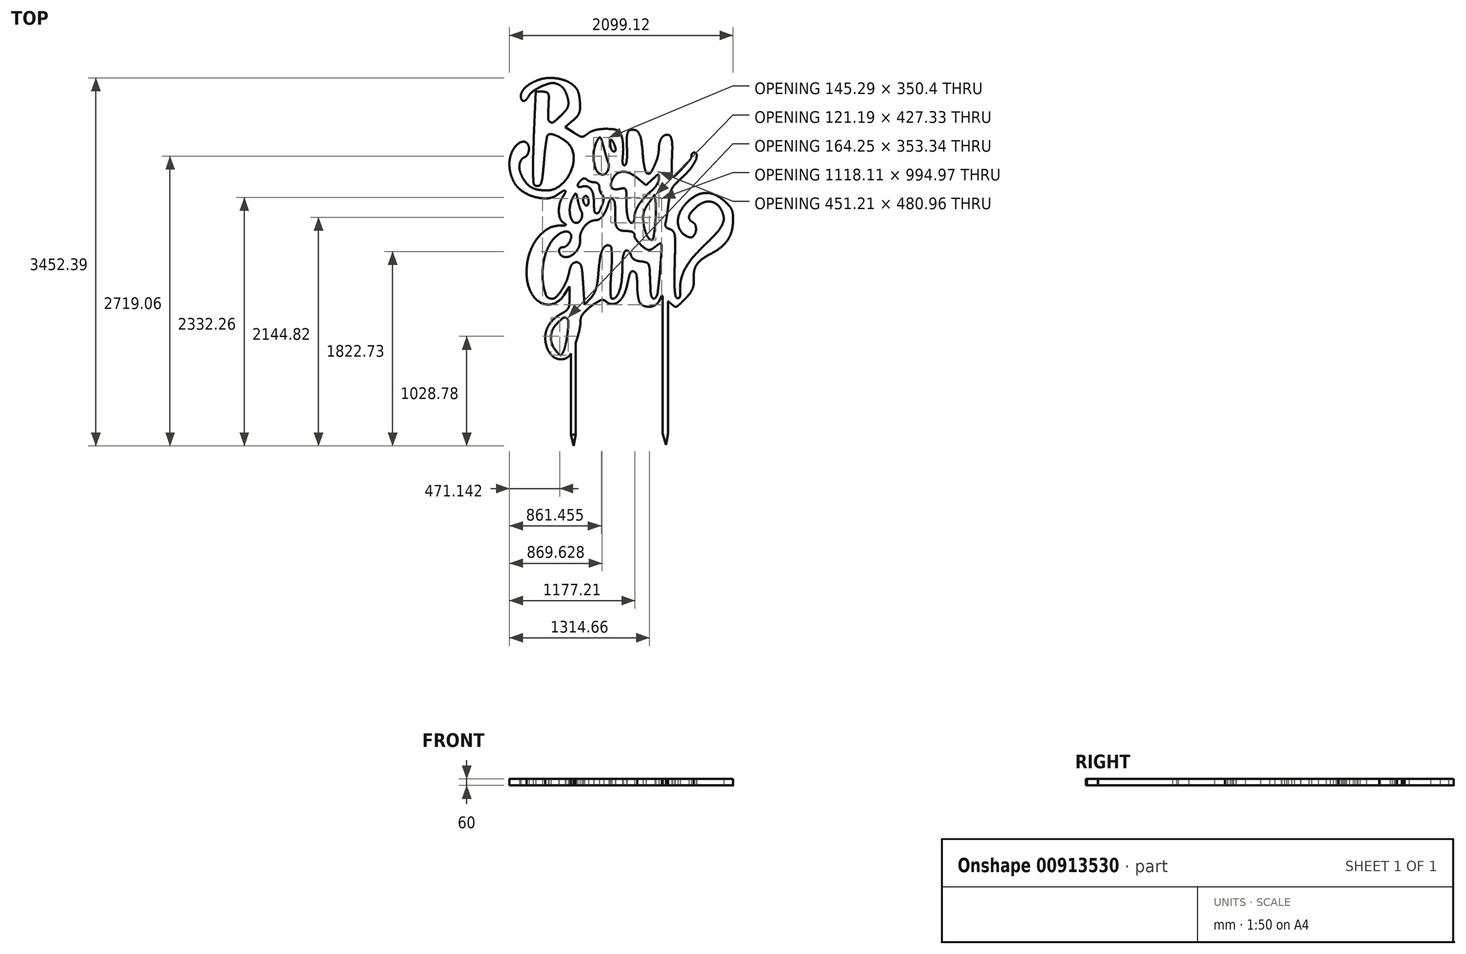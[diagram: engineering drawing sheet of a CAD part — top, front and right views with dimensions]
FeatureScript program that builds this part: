
annotation { "Feature Type Name" : "Feature", "Feature Type Description" : "" }
export const myFeature = defineFeature(function(context is Context, id is Id, definition is map)
    precondition{}
    {
        {
            var Q0;
            Q0=qCreatedBy(makeId("Top.planeOp"),FACE);
            var sketch = newSketch(context, id + "F0", { "sketchPlane" : qUnion([Q0])});
            skArc(sketch, "E0", {"start": v(-777.04, 1301.74) * mm, "mid": v(-811.98, 1287.44) * mm, "end": v(-845.72, 1270.53) * mm});
            skArc(sketch, "E1", {"start": v(-845.72, 1270.53) * mm, "mid": v(-872.99, 1253.32) * mm, "end": v(-897.97, 1232.95) * mm});
            skArc(sketch, "E2", {"start": v(-897.97, 1232.95) * mm, "mid": v(-916, 1213.6) * mm, "end": v(-930.89, 1191.73) * mm});
            skArc(sketch, "E3", {"start": v(-930.89, 1191.73) * mm, "mid": v(-939.28, 1171.38) * mm, "end": v(-942.14, 1149.56) * mm});
            skArc(sketch, "E4", {"start": v(-942.14, 1149.56) * mm, "mid": v(-940.45, 1132.62) * mm, "end": v(-935.44, 1116.36) * mm});
            skArc(sketch, "E5", {"start": v(-935.44, 1116.36) * mm, "mid": v(-928.12, 1107.56) * mm, "end": v(-917.15, 1104.32) * mm});
            skArc(sketch, "E6", {"start": v(-917.15, 1104.32) * mm, "mid": v(-903.56, 1107.28) * mm, "end": v(-892.28, 1115.43) * mm});
            skArc(sketch, "E7", {"start": v(-892.28, 1115.43) * mm, "mid": v(-878.92, 1132.04) * mm, "end": v(-867.72, 1150.18) * mm});
            skArc(sketch, "E8", {"start": v(-867.72, 1150.18) * mm, "mid": v(-849.95, 1175.64) * mm, "end": v(-826.74, 1196.26) * mm});
            skArc(sketch, "E9", {"start": v(-826.74, 1196.26) * mm, "mid": v(-789.65, 1219.77) * mm, "end": v(-750.67, 1240) * mm});
            skArc(sketch, "E10", {"start": v(-750.67, 1240) * mm, "mid": v(-710.75, 1256.5) * mm, "end": v(-669.57, 1269.54) * mm});
            skArc(sketch, "E11", {"start": v(-669.57, 1269.54) * mm, "mid": v(-641.49, 1272.95) * mm, "end": v(-613.58, 1268.31) * mm});
            skArc(sketch, "E12", {"start": v(-613.58, 1268.31) * mm, "mid": v(-592.46, 1259.99) * mm, "end": v(-572.66, 1248.88) * mm});
            skArc(sketch, "E13", {"start": v(-572.66, 1248.88) * mm, "mid": v(-556.03, 1235.87) * mm, "end": v(-541.82, 1220.25) * mm});
            skArc(sketch, "E14", {"start": v(-541.82, 1220.25) * mm, "mid": v(-528.73, 1200.4) * mm, "end": v(-518.57, 1178.9) * mm});
            skArc(sketch, "E15", {"start": v(-518.57, 1178.9) * mm, "mid": v(-508.48, 1150.04) * mm, "end": v(-500.37, 1120.57) * mm});
            skArc(sketch, "E16", {"start": v(-500.37, 1120.57) * mm, "mid": v(-496.82, 1100.94) * mm, "end": v(-495.47, 1081.04) * mm});
            skArc(sketch, "E17", {"start": v(-495.47, 1081.04) * mm, "mid": v(-496.88, 1064.6) * mm, "end": v(-501.45, 1048.76) * mm});
            skArc(sketch, "E18", {"start": v(-501.45, 1048.76) * mm, "mid": v(-509.77, 1031.76) * mm, "end": v(-520.6, 1016.25) * mm});
            skArc(sketch, "E19", {"start": v(-520.6, 1016.25) * mm, "mid": v(-539, 994.92) * mm, "end": v(-558.41, 974.52) * mm});
            skArc(sketch, "E20", {"start": v(-558.41, 974.52) * mm, "mid": v(-594.13, 940.44) * mm, "end": v(-631.42, 908.07) * mm});
            skArc(sketch, "E21", {"start": v(-631.42, 908.07) * mm, "mid": v(-648.14, 901.21) * mm, "end": v(-665.8, 905.07) * mm});
            skArc(sketch, "E22", {"start": v(-665.8, 905.07) * mm, "mid": v(-679.62, 918.6) * mm, "end": v(-684.95, 937.2) * mm});
            skArc(sketch, "E23", {"start": v(-684.95, 937.2) * mm, "mid": v(-685.1, 991.39) * mm, "end": v(-683.23, 1045.54) * mm});
            skArc(sketch, "E24", {"start": v(-683.23, 1045.54) * mm, "mid": v(-681.09, 1091.9) * mm, "end": v(-679.61, 1138.3) * mm});
            skArc(sketch, "E25", {"start": v(-679.61, 1138.3) * mm, "mid": v(-680.84, 1155.14) * mm, "end": v(-685.3, 1171.42) * mm});
            skArc(sketch, "E26", {"start": v(-685.3, 1171.42) * mm, "mid": v(-691.92, 1181.1) * mm, "end": v(-702.22, 1186.72) * mm});
            skArc(sketch, "E27", {"start": v(-702.22, 1186.72) * mm, "mid": v(-720.42, 1190.37) * mm, "end": v(-738.94, 1191.6) * mm});
            skLineSegment(sketch, "E28", {"start": v(-738.94, 1191.6) * mm, "end": v(-802.44, 1191.6) * mm});
            skLineSegment(sketch, "E29", {"start": v(-802.44, 1191.6) * mm, "end": v(-820.4, 760.61) * mm});
            skArc(sketch, "E30", {"start": v(-820.4, 760.61) * mm, "mid": v(-824.35, 656.8) * mm, "end": v(-827.57, 552.97) * mm});
            skArc(sketch, "E31", {"start": v(-827.57, 552.97) * mm, "mid": v(-828.5, 487.7) * mm, "end": v(-827.69, 422.42) * mm});
            skArc(sketch, "E32", {"start": v(-827.69, 422.42) * mm, "mid": v(-825.98, 378.55) * mm, "end": v(-823.12, 334.73) * mm});
            skArc(sketch, "E33", {"start": v(-823.12, 334.73) * mm, "mid": v(-818.8, 321.38) * mm, "end": v(-808.9, 311.44) * mm});
            skArc(sketch, "E34", {"start": v(-808.9, 311.44) * mm, "mid": v(-793.14, 305.84) * mm, "end": v(-776.47, 307.25) * mm});
            skArc(sketch, "E35", {"start": v(-776.47, 307.25) * mm, "mid": v(-762.48, 315.44) * mm, "end": v(-753.63, 329.01) * mm});
            skArc(sketch, "E36", {"start": v(-753.63, 329.01) * mm, "mid": v(-744.19, 361.14) * mm, "end": v(-738.67, 394.16) * mm});
            skArc(sketch, "E37", {"start": v(-738.67, 394.16) * mm, "mid": v(-731.22, 469.42) * mm, "end": v(-724.8, 544.78) * mm});
            skArc(sketch, "E38", {"start": v(-724.8, 544.78) * mm, "mid": v(-721.01, 589.09) * mm, "end": v(-716.56, 633.33) * mm});
            skArc(sketch, "E39", {"start": v(-716.56, 633.33) * mm, "mid": v(-711.98, 671.65) * mm, "end": v(-706.54, 709.86) * mm});
            skArc(sketch, "E40", {"start": v(-706.54, 709.86) * mm, "mid": v(-701.45, 741.63) * mm, "end": v(-695.98, 773.33) * mm});
            skArc(sketch, "E41", {"start": v(-695.98, 773.33) * mm, "mid": v(-693.15, 780.26) * mm, "end": v(-687.74, 785.44) * mm});
            skArc(sketch, "E42", {"start": v(-687.74, 785.44) * mm, "mid": v(-666.87, 792.87) * mm, "end": v(-644.78, 791.07) * mm});
            skArc(sketch, "E43", {"start": v(-644.78, 791.07) * mm, "mid": v(-609.9, 778.58) * mm, "end": v(-576.49, 762.61) * mm});
            skArc(sketch, "E44", {"start": v(-576.49, 762.61) * mm, "mid": v(-542.28, 741.75) * mm, "end": v(-510.37, 717.52) * mm});
            skArc(sketch, "E45", {"start": v(-510.37, 717.52) * mm, "mid": v(-488.03, 694.58) * mm, "end": v(-470.6, 667.72) * mm});
            skArc(sketch, "E46", {"start": v(-470.6, 667.72) * mm, "mid": v(-449.75, 607.16) * mm, "end": v(-447.14, 543.16) * mm});
            skArc(sketch, "E47", {"start": v(-447.14, 543.16) * mm, "mid": v(-462.03, 472.82) * mm, "end": v(-491.08, 407.05) * mm});
            skArc(sketch, "E48", {"start": v(-491.08, 407.05) * mm, "mid": v(-532.53, 349.65) * mm, "end": v(-585.11, 302.23) * mm});
            skArc(sketch, "E49", {"start": v(-585.11, 302.23) * mm, "mid": v(-640.22, 274.16) * mm, "end": v(-701.3, 264.5) * mm});
            skArc(sketch, "E50", {"start": v(-701.3, 264.5) * mm, "mid": v(-741.49, 266.28) * mm, "end": v(-781.36, 271.63) * mm});
            skArc(sketch, "E51", {"start": v(-781.36, 271.63) * mm, "mid": v(-812.7, 280.03) * mm, "end": v(-842.22, 293.53) * mm});
            skArc(sketch, "E52", {"start": v(-842.22, 293.53) * mm, "mid": v(-867.9, 311.17) * mm, "end": v(-890.07, 333.08) * mm});
            skArc(sketch, "E53", {"start": v(-890.07, 333.08) * mm, "mid": v(-911.98, 362.16) * mm, "end": v(-930.5, 393.52) * mm});
            skArc(sketch, "E54", {"start": v(-930.5, 393.52) * mm, "mid": v(-943.45, 422.88) * mm, "end": v(-952.69, 453.62) * mm});
            skArc(sketch, "E55", {"start": v(-952.69, 453.62) * mm, "mid": v(-956.46, 481.2) * mm, "end": v(-955, 508.99) * mm});
            skArc(sketch, "E56", {"start": v(-955, 508.99) * mm, "mid": v(-948.82, 531.69) * mm, "end": v(-937.47, 552.3) * mm});
            skArc(sketch, "E57", {"start": v(-937.47, 552.3) * mm, "mid": v(-922.22, 568.1) * mm, "end": v(-903.08, 578.85) * mm});
            skArc(sketch, "E58", {"start": v(-903.08, 578.85) * mm, "mid": v(-895.32, 583.02) * mm, "end": v(-888.86, 589.01) * mm});
            skArc(sketch, "E59", {"start": v(-888.86, 589.01) * mm, "mid": v(-882.26, 598.03) * mm, "end": v(-876.85, 607.8) * mm});
            skArc(sketch, "E60", {"start": v(-876.85, 607.8) * mm, "mid": v(-872.1, 619.54) * mm, "end": v(-868.7, 631.75) * mm});
            skArc(sketch, "E61", {"start": v(-868.7, 631.75) * mm, "mid": v(-866.64, 644.5) * mm, "end": v(-865.94, 657.4) * mm});
            skArc(sketch, "E62", {"start": v(-865.94, 657.4) * mm, "mid": v(-869.66, 681.72) * mm, "end": v(-880.47, 703.82) * mm});
            skArc(sketch, "E63", {"start": v(-880.47, 703.82) * mm, "mid": v(-896.07, 717.48) * mm, "end": v(-916.26, 722.2) * mm});
            skArc(sketch, "E64", {"start": v(-916.26, 722.2) * mm, "mid": v(-941.99, 717.5) * mm, "end": v(-964.82, 704.74) * mm});
            skArc(sketch, "E65", {"start": v(-964.82, 704.74) * mm, "mid": v(-989.38, 681.71) * mm, "end": v(-1010, 655.1) * mm});
            skArc(sketch, "E66", {"start": v(-1010, 655.1) * mm, "mid": v(-1027.52, 622.95) * mm, "end": v(-1039.6, 588.38) * mm});
            skArc(sketch, "E67", {"start": v(-1039.6, 588.38) * mm, "mid": v(-1047.1, 549.45) * mm, "end": v(-1049.56, 509.88) * mm});
            skArc(sketch, "E68", {"start": v(-1049.56, 509.88) * mm, "mid": v(-1046.94, 468.19) * mm, "end": v(-1039.3, 427.12) * mm});
            skArc(sketch, "E69", {"start": v(-1039.3, 427.12) * mm, "mid": v(-1026.64, 386.66) * mm, "end": v(-1009.39, 347.93) * mm});
            skArc(sketch, "E70", {"start": v(-1009.39, 347.93) * mm, "mid": v(-977.19, 300.5) * mm, "end": v(-934.7, 262) * mm});
            skArc(sketch, "E71", {"start": v(-934.7, 262) * mm, "mid": v(-878.72, 228.84) * mm, "end": v(-818.08, 205.25) * mm});
            skArc(sketch, "E72", {"start": v(-818.08, 205.25) * mm, "mid": v(-756.67, 192.57) * mm, "end": v(-694, 190.48) * mm});
            skArc(sketch, "E73", {"start": v(-694, 190.48) * mm, "mid": v(-643.24, 200.81) * mm, "end": v(-597.75, 225.59) * mm});
            skArc(sketch, "E74", {"start": v(-597.75, 225.59) * mm, "mid": v(-574.17, 242.72) * mm, "end": v(-549.96, 258.94) * mm});
            skArc(sketch, "E75", {"start": v(-549.96, 258.94) * mm, "mid": v(-539.4, 262.73) * mm, "end": v(-528.26, 261.53) * mm});
            skArc(sketch, "E76", {"start": v(-528.26, 261.53) * mm, "mid": v(-522.4, 255.93) * mm, "end": v(-522.82, 247.84) * mm});
            skArc(sketch, "E77", {"start": v(-522.82, 247.84) * mm, "mid": v(-534.26, 227.55) * mm, "end": v(-547, 208.04) * mm});
            skArc(sketch, "E78", {"start": v(-547, 208.04) * mm, "mid": v(-564.68, 177.38) * mm, "end": v(-576.72, 144.1) * mm});
            skArc(sketch, "E79", {"start": v(-576.72, 144.1) * mm, "mid": v(-583.92, 106.5) * mm, "end": v(-585.83, 68.26) * mm});
            skArc(sketch, "E80", {"start": v(-585.83, 68.26) * mm, "mid": v(-582.5, 34.05) * mm, "end": v(-573.99, 0.75) * mm});
            skArc(sketch, "E81", {"start": v(-573.99, 0.75) * mm, "mid": v(-561.57, -21.65) * mm, "end": v(-542.1, -38.27) * mm});
            skArc(sketch, "E82", {"start": v(-542.1, -38.27) * mm, "mid": v(-531.5, -44.9) * mm, "end": v(-521.34, -52.18) * mm});
            skArc(sketch, "E83", {"start": v(-521.34, -52.18) * mm, "mid": v(-519.57, -55.83) * mm, "end": v(-521.45, -59.42) * mm});
            skArc(sketch, "E84", {"start": v(-521.45, -59.42) * mm, "mid": v(-527.58, -62.58) * mm, "end": v(-534.35, -63.84) * mm});
            skArc(sketch, "E85", {"start": v(-534.35, -63.84) * mm, "mid": v(-556.83, -64.56) * mm, "end": v(-579.31, -64.93) * mm});
            skArc(sketch, "E86", {"start": v(-579.31, -64.93) * mm, "mid": v(-646.05, -75.84) * mm, "end": v(-706.44, -106.29) * mm});
            skArc(sketch, "E87", {"start": v(-706.44, -106.29) * mm, "mid": v(-765.07, -157.71) * mm, "end": v(-812.24, -219.8) * mm});
            skArc(sketch, "E88", {"start": v(-812.24, -219.8) * mm, "mid": v(-851.5, -298.55) * mm, "end": v(-876.57, -382.89) * mm});
            skArc(sketch, "E89", {"start": v(-876.57, -382.89) * mm, "mid": v(-887.79, -473.12) * mm, "end": v(-884.73, -564) * mm});
            skArc(sketch, "E90", {"start": v(-884.73, -564) * mm, "mid": v(-868.69, -638.22) * mm, "end": v(-838.12, -707.72) * mm});
            skArc(sketch, "E91", {"start": v(-838.12, -707.72) * mm, "mid": v(-797.57, -758.57) * mm, "end": v(-743.21, -794.27) * mm});
            skArc(sketch, "E92", {"start": v(-743.21, -794.27) * mm, "mid": v(-688.13, -806.79) * mm, "end": v(-632.5, -796.92) * mm});
            skArc(sketch, "E93", {"start": v(-632.5, -796.92) * mm, "mid": v(-579.5, -765.74) * mm, "end": v(-538.67, -719.76) * mm});
            skLineSegment(sketch, "E94", {"start": v(-538.67, -719.76) * mm, "end": v(-485.8, -637.2) * mm});
            skLineSegment(sketch, "E95", {"start": v(-485.8, -637.2) * mm, "end": v(-485.37, -744.5) * mm});
            skArc(sketch, "E96", {"start": v(-485.37, -744.5) * mm, "mid": v(-485.96, -774.69) * mm, "end": v(-487.95, -804.81) * mm});
            skArc(sketch, "E97", {"start": v(-487.95, -804.81) * mm, "mid": v(-491.3, -822.8) * mm, "end": v(-498.02, -839.84) * mm});
            skArc(sketch, "E98", {"start": v(-498.02, -839.84) * mm, "mid": v(-507.23, -853.74) * mm, "end": v(-519.35, -865.2) * mm});
            skArc(sketch, "E99", {"start": v(-519.35, -865.2) * mm, "mid": v(-538.96, -878.63) * mm, "end": v(-559.6, -890.4) * mm});
            skArc(sketch, "E100", {"start": v(-559.6, -890.4) * mm, "mid": v(-593.01, -910.11) * mm, "end": v(-624.03, -933.4) * mm});
            skArc(sketch, "E101", {"start": v(-624.03, -933.4) * mm, "mid": v(-650.22, -958.64) * mm, "end": v(-672.8, -987.17) * mm});
            skArc(sketch, "E102", {"start": v(-672.8, -987.17) * mm, "mid": v(-690.18, -1016.83) * mm, "end": v(-703.13, -1048.68) * mm});
            skArc(sketch, "E103", {"start": v(-703.13, -1048.68) * mm, "mid": v(-710.93, -1081.15) * mm, "end": v(-713.54, -1114.43) * mm});
            skArc(sketch, "E104", {"start": v(-713.54, -1114.43) * mm, "mid": v(-709.25, -1164.27) * mm, "end": v(-696.48, -1212.64) * mm});
            skArc(sketch, "E105", {"start": v(-696.48, -1212.64) * mm, "mid": v(-676.44, -1252.77) * mm, "end": v(-647.53, -1287.07) * mm});
            skArc(sketch, "E106", {"start": v(-647.53, -1287.07) * mm, "mid": v(-616.27, -1308.39) * mm, "end": v(-580.03, -1319.28) * mm});
            skArc(sketch, "E107", {"start": v(-580.03, -1319.28) * mm, "mid": v(-543.8, -1318.03) * mm, "end": v(-510.15, -1304.54) * mm});
            skArc(sketch, "E108", {"start": v(-510.15, -1304.54) * mm, "mid": v(-486.73, -1285.12) * mm, "end": v(-469.45, -1260.08) * mm});
            skArc(sketch, "E109", {"start": v(-469.45, -1260.08) * mm, "mid": v(-446.77, -1211.64) * mm, "end": v(-426.9, -1161.97) * mm});
            skArc(sketch, "E110", {"start": v(-426.9, -1161.97) * mm, "mid": v(-408.73, -1107.29) * mm, "end": v(-393.98, -1051.58) * mm});
            skArc(sketch, "E111", {"start": v(-393.98, -1051.58) * mm, "mid": v(-385.64, -1004.33) * mm, "end": v(-382.38, -956.45) * mm});
            skArc(sketch, "E112", {"start": v(-382.38, -956.45) * mm, "mid": v(-375.86, -922.1) * mm, "end": v(-358.1, -891.99) * mm});
            skArc(sketch, "E113", {"start": v(-358.1, -891.99) * mm, "mid": v(-321.43, -853.25) * mm, "end": v(-280.92, -818.55) * mm});
            skArc(sketch, "E114", {"start": v(-280.92, -818.55) * mm, "mid": v(-239.63, -790.17) * mm, "end": v(-195.52, -766.4) * mm});
            skArc(sketch, "E115", {"start": v(-195.52, -766.4) * mm, "mid": v(-169.69, -762.92) * mm, "end": v(-146.56, -774.94) * mm});
            skArc(sketch, "E116", {"start": v(-146.56, -774.94) * mm, "mid": v(-119.03, -793.63) * mm, "end": v(-86.55, -800.87) * mm});
            skArc(sketch, "E117", {"start": v(-86.55, -800.87) * mm, "mid": v(-53.59, -795.67) * mm, "end": v(-24.8, -778.77) * mm});
            skArc(sketch, "E118", {"start": v(-24.8, -778.77) * mm, "mid": v(6.07, -744.96) * mm, "end": v(28.55, -705.07) * mm});
            skArc(sketch, "E119", {"start": v(28.55, -705.07) * mm, "mid": v(48.4, -649.83) * mm, "end": v(62.1, -592.76) * mm});
            skArc(sketch, "E120", {"start": v(62.1, -592.76) * mm, "mid": v(71.96, -549.68) * mm, "end": v(85.6, -507.64) * mm});
            skArc(sketch, "E121", {"start": v(85.6, -507.64) * mm, "mid": v(98.21, -494.53) * mm, "end": v(116.4, -494.75) * mm});
            skArc(sketch, "E122", {"start": v(116.4, -494.75) * mm, "mid": v(134.63, -509.35) * mm, "end": v(143.41, -530.98) * mm});
            skArc(sketch, "E123", {"start": v(143.41, -530.98) * mm, "mid": v(148.4, -581.45) * mm, "end": v(150.06, -632.13) * mm});
            skArc(sketch, "E124", {"start": v(150.06, -632.13) * mm, "mid": v(150.61, -659.04) * mm, "end": v(152.3, -685.9) * mm});
            skArc(sketch, "E125", {"start": v(152.3, -685.9) * mm, "mid": v(155.03, -711.11) * mm, "end": v(159, -736.16) * mm});
            skArc(sketch, "E126", {"start": v(159, -736.16) * mm, "mid": v(163.35, -756.8) * mm, "end": v(168.71, -777.21) * mm});
            skArc(sketch, "E127", {"start": v(168.71, -777.21) * mm, "mid": v(173.36, -787.97) * mm, "end": v(180.54, -797.23) * mm});
            skArc(sketch, "E128", {"start": v(180.54, -797.23) * mm, "mid": v(199.82, -812.2) * mm, "end": v(222.2, -821.92) * mm});
            skArc(sketch, "E129", {"start": v(222.2, -821.92) * mm, "mid": v(247.82, -826.6) * mm, "end": v(273.85, -825.91) * mm});
            skArc(sketch, "E130", {"start": v(273.85, -825.91) * mm, "mid": v(298.9, -819.92) * mm, "end": v(322.15, -808.84) * mm});
            skArc(sketch, "E131", {"start": v(322.15, -808.84) * mm, "mid": v(340.63, -793.84) * mm, "end": v(354.53, -774.52) * mm});
            skLineSegment(sketch, "E132", {"start": v(354.53, -774.52) * mm, "end": v(383, -721.33) * mm});
            skLineSegment(sketch, "E133", {"start": v(383, -721.33) * mm, "end": v(439.61, -774.52) * mm});
            skArc(sketch, "E134", {"start": v(439.61, -774.52) * mm, "mid": v(450.9, -784.86) * mm, "end": v(462.47, -794.89) * mm});
            skArc(sketch, "E135", {"start": v(462.47, -794.89) * mm, "mid": v(473.25, -803.68) * mm, "end": v(484.34, -812.08) * mm});
            skArc(sketch, "E136", {"start": v(484.34, -812.08) * mm, "mid": v(493.65, -818.68) * mm, "end": v(503.16, -825) * mm});
            skArc(sketch, "E137", {"start": v(503.16, -825) * mm, "mid": v(507.56, -827.02) * mm, "end": v(512.35, -827.7) * mm});
            skArc(sketch, "E138", {"start": v(512.35, -827.7) * mm, "mid": v(517.45, -826.83) * mm, "end": v(521.96, -824.3) * mm});
            skArc(sketch, "E139", {"start": v(521.96, -824.3) * mm, "mid": v(534.45, -814) * mm, "end": v(546.74, -803.46) * mm});
            skArc(sketch, "E140", {"start": v(546.74, -803.46) * mm, "mid": v(561.35, -790.32) * mm, "end": v(575.6, -776.78) * mm});
            skArc(sketch, "E141", {"start": v(575.6, -776.78) * mm, "mid": v(591.33, -761.12) * mm, "end": v(606.76, -745.16) * mm});
            skArc(sketch, "E142", {"start": v(606.76, -745.16) * mm, "mid": v(625.4, -724.36) * mm, "end": v(642.84, -702.54) * mm});
            skArc(sketch, "E143", {"start": v(642.84, -702.54) * mm, "mid": v(655.37, -683.92) * mm, "end": v(665.83, -664.07) * mm});
            skArc(sketch, "E144", {"start": v(665.83, -664.07) * mm, "mid": v(672.93, -645.6) * mm, "end": v(677.63, -626.38) * mm});
            skArc(sketch, "E145", {"start": v(677.63, -626.38) * mm, "mid": v(679.92, -606.46) * mm, "end": v(679.77, -586.4) * mm});
            skArc(sketch, "E146", {"start": v(679.77, -586.4) * mm, "mid": v(679.01, -543.04) * mm, "end": v(682.73, -499.83) * mm});
            skArc(sketch, "E147", {"start": v(682.73, -499.83) * mm, "mid": v(690.9, -466.46) * mm, "end": v(705.67, -435.44) * mm});
            skArc(sketch, "E148", {"start": v(705.67, -435.44) * mm, "mid": v(727.03, -406.96) * mm, "end": v(753.45, -383.1) * mm});
            skArc(sketch, "E149", {"start": v(753.45, -383.1) * mm, "mid": v(792.57, -356.58) * mm, "end": v(833.78, -333.46) * mm});
            skArc(sketch, "E150", {"start": v(833.78, -333.46) * mm, "mid": v(883.51, -305.27) * mm, "end": v(930.4, -272.56) * mm});
            skArc(sketch, "E151", {"start": v(930.4, -272.56) * mm, "mid": v(966.1, -240.37) * mm, "end": v(996.36, -203.02) * mm});
            skArc(sketch, "E152", {"start": v(996.36, -203.02) * mm, "mid": v(1019.08, -163.28) * mm, "end": v(1034.87, -120.31) * mm});
            skArc(sketch, "E153", {"start": v(1034.87, -120.31) * mm, "mid": v(1045.26, -70.74) * mm, "end": v(1049.44, -20.27) * mm});
            skArc(sketch, "E154", {"start": v(1049.44, -20.27) * mm, "mid": v(1049.21, 10.95) * mm, "end": v(1047.22, 42.11) * mm});
            skArc(sketch, "E155", {"start": v(1047.22, 42.11) * mm, "mid": v(1043.5, 63.58) * mm, "end": v(1036.42, 84.18) * mm});
            skArc(sketch, "E156", {"start": v(1036.42, 84.18) * mm, "mid": v(1026.16, 103.41) * mm, "end": v(1012.98, 120.77) * mm});
            skArc(sketch, "E157", {"start": v(1012.98, 120.77) * mm, "mid": v(991.51, 143.49) * mm, "end": v(968.8, 164.96) * mm});
            skArc(sketch, "E158", {"start": v(968.8, 164.96) * mm, "mid": v(926.55, 197.47) * mm, "end": v(879.98, 223.43) * mm});
            skArc(sketch, "E159", {"start": v(879.98, 223.43) * mm, "mid": v(836.76, 237.63) * mm, "end": v(791.42, 241.38) * mm});
            skArc(sketch, "E160", {"start": v(791.42, 241.38) * mm, "mid": v(746.16, 234.5) * mm, "end": v(703.71, 217.35) * mm});
            skArc(sketch, "E161", {"start": v(703.71, 217.35) * mm, "mid": v(658.26, 188.13) * mm, "end": v(617.42, 152.73) * mm});
            skArc(sketch, "E162", {"start": v(617.42, 152.73) * mm, "mid": v(580.16, 108.54) * mm, "end": v(550.91, 58.69) * mm});
            skArc(sketch, "E163", {"start": v(550.91, 58.69) * mm, "mid": v(535.03, 10.7) * mm, "end": v(531.63, -39.74) * mm});
            skArc(sketch, "E164", {"start": v(531.63, -39.74) * mm, "mid": v(540.99, -83.45) * mm, "end": v(563, -122.35) * mm});
            skArc(sketch, "E165", {"start": v(563, -122.35) * mm, "mid": v(596.07, -153.86) * mm, "end": v(636.68, -174.77) * mm});
            skArc(sketch, "E166", {"start": v(636.68, -174.77) * mm, "mid": v(656.04, -175.89) * mm, "end": v(673.13, -166.73) * mm});
            skArc(sketch, "E167", {"start": v(673.13, -166.73) * mm, "mid": v(688.46, -147.18) * mm, "end": v(697.85, -124.19) * mm});
            skArc(sketch, "E168", {"start": v(697.85, -124.19) * mm, "mid": v(701.45, -97) * mm, "end": v(698.6, -69.74) * mm});
            skArc(sketch, "E169", {"start": v(698.6, -69.74) * mm, "mid": v(689.21, -49.38) * mm, "end": v(672.35, -34.6) * mm});
            skArc(sketch, "E170", {"start": v(672.35, -34.6) * mm, "mid": v(656.54, -23.67) * mm, "end": v(643.07, -9.97) * mm});
            skArc(sketch, "E171", {"start": v(643.07, -9.97) * mm, "mid": v(636.5, 2.93) * mm, "end": v(635.84, 17.38) * mm});
            skArc(sketch, "E172", {"start": v(635.84, 17.38) * mm, "mid": v(641.31, 35.49) * mm, "end": v(651.17, 51.63) * mm});
            skArc(sketch, "E173", {"start": v(651.17, 51.63) * mm, "mid": v(672.42, 76.69) * mm, "end": v(695, 100.55) * mm});
            skArc(sketch, "E174", {"start": v(695, 100.55) * mm, "mid": v(723.42, 124.87) * mm, "end": v(755.26, 144.5) * mm});
            skArc(sketch, "E175", {"start": v(755.26, 144.5) * mm, "mid": v(786.12, 156.21) * mm, "end": v(818.8, 160.76) * mm});
            skArc(sketch, "E176", {"start": v(818.8, 160.76) * mm, "mid": v(848.86, 157.68) * mm, "end": v(877.17, 147.12) * mm});
            skArc(sketch, "E177", {"start": v(877.17, 147.12) * mm, "mid": v(902.67, 129.53) * mm, "end": v(923.31, 106.44) * mm});
            skArc(sketch, "E178", {"start": v(923.31, 106.44) * mm, "mid": v(944.5, 69.3) * mm, "end": v(958.48, 28.88) * mm});
            skArc(sketch, "E179", {"start": v(958.48, 28.88) * mm, "mid": v(961.62, -7.02) * mm, "end": v(953.81, -42.2) * mm});
            skArc(sketch, "E180", {"start": v(953.81, -42.2) * mm, "mid": v(932.47, -85.07) * mm, "end": v(903.73, -123.38) * mm});
            skArc(sketch, "E181", {"start": v(903.73, -123.38) * mm, "mid": v(846.78, -184.04) * mm, "end": v(787.51, -242.43) * mm});
            skArc(sketch, "E182", {"start": v(787.51, -242.43) * mm, "mid": v(727.95, -301.88) * mm, "end": v(671.55, -364.32) * mm});
            skArc(sketch, "E183", {"start": v(671.55, -364.32) * mm, "mid": v(631.94, -416) * mm, "end": v(598.24, -471.71) * mm});
            skArc(sketch, "E184", {"start": v(598.24, -471.71) * mm, "mid": v(575.71, -522.14) * mm, "end": v(560.32, -575.18) * mm});
            skArc(sketch, "E185", {"start": v(560.32, -575.18) * mm, "mid": v(552.55, -629.3) * mm, "end": v(552.52, -683.97) * mm});
            skArc(sketch, "E186", {"start": v(552.52, -683.97) * mm, "mid": v(553.2, -699.86) * mm, "end": v(553.03, -715.77) * mm});
            skArc(sketch, "E187", {"start": v(553.03, -715.77) * mm, "mid": v(551.67, -725.91) * mm, "end": v(548.4, -735.62) * mm});
            skArc(sketch, "E188", {"start": v(548.4, -735.62) * mm, "mid": v(544.55, -741.08) * mm, "end": v(538.9, -744.69) * mm});
            skArc(sketch, "E189", {"start": v(538.9, -744.69) * mm, "mid": v(532.12, -746.04) * mm, "end": v(525.28, -744.97) * mm});
            skArc(sketch, "E190", {"start": v(525.28, -744.97) * mm, "mid": v(514.91, -737.95) * mm, "end": v(509.44, -726.68) * mm});
            skArc(sketch, "E191", {"start": v(509.44, -726.68) * mm, "mid": v(504.8, -698) * mm, "end": v(501.84, -669.1) * mm});
            skArc(sketch, "E192", {"start": v(501.84, -669.1) * mm, "mid": v(499.42, -623.07) * mm, "end": v(498.88, -576.99) * mm});
            skArc(sketch, "E193", {"start": v(498.88, -576.99) * mm, "mid": v(499.93, -500.2) * mm, "end": v(501.72, -423.41) * mm});
            skArc(sketch, "E194", {"start": v(501.72, -423.41) * mm, "mid": v(504.22, -324.89) * mm, "end": v(506.15, -226.35) * mm});
            skArc(sketch, "E195", {"start": v(506.15, -226.35) * mm, "mid": v(505.35, -190.22) * mm, "end": v(501.76, -154.26) * mm});
            skArc(sketch, "E196", {"start": v(501.76, -154.26) * mm, "mid": v(496.55, -135.43) * mm, "end": v(486.6, -118.6) * mm});
            skArc(sketch, "E197", {"start": v(486.6, -118.6) * mm, "mid": v(473.2, -106.3) * mm, "end": v(456.56, -98.91) * mm});
            skArc(sketch, "E198", {"start": v(456.56, -98.91) * mm, "mid": v(445.17, -95.22) * mm, "end": v(434.28, -90.23) * mm});
            skArc(sketch, "E199", {"start": v(434.28, -90.23) * mm, "mid": v(426.28, -84.8) * mm, "end": v(419.64, -77.78) * mm});
            skArc(sketch, "E200", {"start": v(419.64, -77.78) * mm, "mid": v(415.36, -70.3) * mm, "end": v(413.15, -61.99) * mm});
            skArc(sketch, "E201", {"start": v(413.15, -61.99) * mm, "mid": v(412.89, -52.68) * mm, "end": v(414.53, -43.5) * mm});
            skArc(sketch, "E202", {"start": v(414.53, -43.5) * mm, "mid": v(417.67, -31.4) * mm, "end": v(420.14, -19.13) * mm});
            skArc(sketch, "E203", {"start": v(420.14, -19.13) * mm, "mid": v(424.16, 4.69) * mm, "end": v(427.97, 28.54) * mm});
            skArc(sketch, "E204", {"start": v(427.97, 28.54) * mm, "mid": v(432.2, 56.68) * mm, "end": v(436.13, 84.86) * mm});
            skArc(sketch, "E205", {"start": v(436.13, 84.86) * mm, "mid": v(439.98, 114.3) * mm, "end": v(443.56, 143.77) * mm});
            skArc(sketch, "E206", {"start": v(443.56, 143.77) * mm, "mid": v(449.23, 185.04) * mm, "end": v(456.5, 226.06) * mm});
            skArc(sketch, "E207", {"start": v(456.5, 226.06) * mm, "mid": v(463.55, 252.67) * mm, "end": v(473.93, 278.17) * mm});
            skArc(sketch, "E208", {"start": v(473.93, 278.17) * mm, "mid": v(486.82, 300.55) * mm, "end": v(502.8, 320.86) * mm});
            skArc(sketch, "E209", {"start": v(502.8, 320.86) * mm, "mid": v(527.19, 346.14) * mm, "end": v(553.02, 369.94) * mm});
            skArc(sketch, "E210", {"start": v(553.02, 369.94) * mm, "mid": v(596.42, 410.44) * mm, "end": v(636.82, 453.93) * mm});
            skArc(sketch, "E211", {"start": v(636.82, 453.93) * mm, "mid": v(667.52, 493.92) * mm, "end": v(693.38, 537.2) * mm});
            skArc(sketch, "E212", {"start": v(693.38, 537.2) * mm, "mid": v(704.1, 565.44) * mm, "end": v(707.92, 595.42) * mm});
            skArc(sketch, "E213", {"start": v(707.92, 595.42) * mm, "mid": v(700.83, 612.85) * mm, "end": v(683.46, 620.1) * mm});
            skArc(sketch, "E214", {"start": v(683.46, 620.1) * mm, "mid": v(678.45, 619.44) * mm, "end": v(673.77, 617.54) * mm});
            skArc(sketch, "E215", {"start": v(673.77, 617.54) * mm, "mid": v(669.28, 614.37) * mm, "end": v(665.52, 610.36) * mm});
            skArc(sketch, "E216", {"start": v(665.52, 610.36) * mm, "mid": v(662.26, 605.24) * mm, "end": v(659.97, 599.63) * mm});
            skArc(sketch, "E217", {"start": v(659.97, 599.63) * mm, "mid": v(658.54, 593.37) * mm, "end": v(658.06, 586.98) * mm});
            skArc(sketch, "E218", {"start": v(658.06, 586.98) * mm, "mid": v(655.02, 569.8) * mm, "end": v(646.29, 554.68) * mm});
            skArc(sketch, "E219", {"start": v(646.29, 554.68) * mm, "mid": v(612.9, 515.86) * mm, "end": v(578.67, 477.79) * mm});
            skArc(sketch, "E220", {"start": v(578.67, 477.79) * mm, "mid": v(543.45, 440.31) * mm, "end": v(507.46, 403.6) * mm});
            skArc(sketch, "E221", {"start": v(507.46, 403.6) * mm, "mid": v(494.04, 394.64) * mm, "end": v(478.22, 391.5) * mm});
            skArc(sketch, "E222", {"start": v(478.22, 391.5) * mm, "mid": v(474.94, 392.82) * mm, "end": v(473.52, 396.05) * mm});
            skArc(sketch, "E223", {"start": v(473.52, 396.05) * mm, "mid": v(472.9, 420.2) * mm, "end": v(472.5, 444.34) * mm});
            skArc(sketch, "E224", {"start": v(472.5, 444.34) * mm, "mid": v(472.46, 473.38) * mm, "end": v(473.05, 502.4) * mm});
            skArc(sketch, "E225", {"start": v(473.05, 502.4) * mm, "mid": v(474.33, 536.9) * mm, "end": v(476.06, 571.39) * mm});
            skArc(sketch, "E226", {"start": v(476.06, 571.39) * mm, "mid": v(478.43, 634.44) * mm, "end": v(478.41, 697.53) * mm});
            skArc(sketch, "E227", {"start": v(478.41, 697.53) * mm, "mid": v(474.43, 732.8) * mm, "end": v(463.97, 766.71) * mm});
            skArc(sketch, "E228", {"start": v(463.97, 766.71) * mm, "mid": v(452.07, 781.5) * mm, "end": v(434.08, 787.52) * mm});
            skArc(sketch, "E229", {"start": v(434.08, 787.52) * mm, "mid": v(411.95, 784.3) * mm, "end": v(392.43, 773.39) * mm});
            skArc(sketch, "E230", {"start": v(392.43, 773.39) * mm, "mid": v(384.13, 765.17) * mm, "end": v(377.4, 755.62) * mm});
            skArc(sketch, "E231", {"start": v(377.4, 755.62) * mm, "mid": v(370.5, 742.44) * mm, "end": v(364.76, 728.71) * mm});
            skArc(sketch, "E232", {"start": v(364.76, 728.71) * mm, "mid": v(359.82, 713.36) * mm, "end": v(356.15, 697.65) * mm});
            skArc(sketch, "E233", {"start": v(356.15, 697.65) * mm, "mid": v(353.98, 682.38) * mm, "end": v(353.26, 666.97) * mm});
            skArc(sketch, "E234", {"start": v(353.26, 666.97) * mm, "mid": v(350.8, 626.9) * mm, "end": v(343.49, 587.42) * mm});
            skArc(sketch, "E235", {"start": v(343.49, 587.42) * mm, "mid": v(330.67, 544.01) * mm, "end": v(314.2, 501.86) * mm});
            skArc(sketch, "E236", {"start": v(314.2, 501.86) * mm, "mid": v(297.1, 467.12) * mm, "end": v(277.15, 433.95) * mm});
            skArc(sketch, "E237", {"start": v(277.15, 433.95) * mm, "mid": v(263.26, 423.14) * mm, "end": v(245.67, 423) * mm});
            skArc(sketch, "E238", {"start": v(245.67, 423) * mm, "mid": v(236.8, 428.37) * mm, "end": v(231.15, 437.07) * mm});
            skArc(sketch, "E239", {"start": v(231.15, 437.07) * mm, "mid": v(224.26, 457.87) * mm, "end": v(218.67, 479.06) * mm});
            skArc(sketch, "E240", {"start": v(218.67, 479.06) * mm, "mid": v(212.66, 508.7) * mm, "end": v(208.25, 538.6) * mm});
            skArc(sketch, "E241", {"start": v(208.25, 538.6) * mm, "mid": v(204.06, 577.6) * mm, "end": v(200.86, 616.7) * mm});
            skArc(sketch, "E242", {"start": v(200.86, 616.7) * mm, "mid": v(195.44, 676.56) * mm, "end": v(187.5, 736.13) * mm});
            skArc(sketch, "E243", {"start": v(187.5, 736.13) * mm, "mid": v(178.87, 770.96) * mm, "end": v(164.16, 803.69) * mm});
            skArc(sketch, "E244", {"start": v(164.16, 803.69) * mm, "mid": v(149.24, 821.3) * mm, "end": v(128.81, 832.05) * mm});
            skArc(sketch, "E245", {"start": v(128.81, 832.05) * mm, "mid": v(104.7, 835.17) * mm, "end": v(80.88, 830.3) * mm});
            skArc(sketch, "E246", {"start": v(80.88, 830.3) * mm, "mid": v(71.26, 824.37) * mm, "end": v(64.45, 815.35) * mm});
            skArc(sketch, "E247", {"start": v(64.45, 815.35) * mm, "mid": v(58.57, 800.91) * mm, "end": v(54.88, 785.76) * mm});
            skArc(sketch, "E248", {"start": v(54.88, 785.76) * mm, "mid": v(51.96, 762.1) * mm, "end": v(51.06, 738.26) * mm});
            skArc(sketch, "E249", {"start": v(51.06, 738.26) * mm, "mid": v(51.67, 701.01) * mm, "end": v(53.17, 663.79) * mm});
            skArc(sketch, "E250", {"start": v(53.17, 663.79) * mm, "mid": v(54.44, 630.86) * mm, "end": v(54.8, 597.9) * mm});
            skArc(sketch, "E251", {"start": v(54.8, 597.9) * mm, "mid": v(53.97, 573) * mm, "end": v(51.58, 548.18) * mm});
            skArc(sketch, "E252", {"start": v(51.58, 548.18) * mm, "mid": v(48.67, 530.75) * mm, "end": v(44.42, 513.6) * mm});
            skArc(sketch, "E253", {"start": v(44.42, 513.6) * mm, "mid": v(39.95, 505.8) * mm, "end": v(32.4, 500.91) * mm});
            skArc(sketch, "E254", {"start": v(32.4, 500.91) * mm, "mid": v(26.05, 500.71) * mm, "end": v(20.73, 504.2) * mm});
            skArc(sketch, "E255", {"start": v(20.73, 504.2) * mm, "mid": v(16.12, 511.58) * mm, "end": v(13.56, 519.9) * mm});
            skArc(sketch, "E256", {"start": v(13.56, 519.9) * mm, "mid": v(11.78, 535.41) * mm, "end": v(11.7, 551.02) * mm});
            skArc(sketch, "E257", {"start": v(11.7, 551.02) * mm, "mid": v(13.26, 575.5) * mm, "end": v(15.56, 599.92) * mm});
            skArc(sketch, "E258", {"start": v(15.56, 599.92) * mm, "mid": v(17.5, 623.18) * mm, "end": v(18.26, 646.5) * mm});
            skArc(sketch, "E259", {"start": v(18.26, 646.5) * mm, "mid": v(17.9, 671.41) * mm, "end": v(16.5, 696.28) * mm});
            skArc(sketch, "E260", {"start": v(16.5, 696.28) * mm, "mid": v(14.24, 719.16) * mm, "end": v(11, 741.93) * mm});
            skArc(sketch, "E261", {"start": v(11, 741.93) * mm, "mid": v(7.36, 758.59) * mm, "end": v(2.04, 774.79) * mm});
            skArc(sketch, "E262", {"start": v(2.04, 774.79) * mm, "mid": v(-6.22, 792.93) * mm, "end": v(-16.54, 809.98) * mm});
            skArc(sketch, "E263", {"start": v(-16.54, 809.98) * mm, "mid": v(-26.64, 821.2) * mm, "end": v(-39.3, 829.4) * mm});
            skArc(sketch, "E264", {"start": v(-39.3, 829.4) * mm, "mid": v(-56.51, 835.78) * mm, "end": v(-74.59, 839) * mm});
            skArc(sketch, "E265", {"start": v(-74.59, 839) * mm, "mid": v(-107.21, 841.26) * mm, "end": v(-139.9, 842.34) * mm});
            skArc(sketch, "E266", {"start": v(-139.9, 842.34) * mm, "mid": v(-166.64, 842.02) * mm, "end": v(-193.33, 840.24) * mm});
            skArc(sketch, "E267", {"start": v(-193.33, 840.24) * mm, "mid": v(-217.1, 837.1) * mm, "end": v(-240.55, 832.18) * mm});
            skArc(sketch, "E268", {"start": v(-240.55, 832.18) * mm, "mid": v(-260.75, 826.22) * mm, "end": v(-280.35, 818.53) * mm});
            skArc(sketch, "E269", {"start": v(-280.35, 818.53) * mm, "mid": v(-296.5, 810.08) * mm, "end": v(-311.38, 799.57) * mm});
            skArc(sketch, "E270", {"start": v(-311.38, 799.57) * mm, "mid": v(-328.57, 786.53) * mm, "end": v(-346.54, 774.59) * mm});
            skArc(sketch, "E271", {"start": v(-346.54, 774.59) * mm, "mid": v(-357.73, 769.85) * mm, "end": v(-369.83, 768.73) * mm});
            skArc(sketch, "E272", {"start": v(-369.83, 768.73) * mm, "mid": v(-383.23, 771.14) * mm, "end": v(-395.7, 776.58) * mm});
            skArc(sketch, "E273", {"start": v(-395.7, 776.58) * mm, "mid": v(-421.04, 791.84) * mm, "end": v(-445.91, 807.84) * mm});
            skLineSegment(sketch, "E274", {"start": v(-445.91, 807.84) * mm, "end": v(-525.44, 860.64) * mm});
            skLineSegment(sketch, "E275", {"start": v(-525.44, 860.64) * mm, "end": v(-453.14, 921.48) * mm});
            skArc(sketch, "E276", {"start": v(-453.14, 921.48) * mm, "mid": v(-433.13, 939.56) * mm, "end": v(-414.44, 959) * mm});
            skArc(sketch, "E277", {"start": v(-414.44, 959) * mm, "mid": v(-403.05, 974.43) * mm, "end": v(-394.75, 991.72) * mm});
            skArc(sketch, "E278", {"start": v(-394.75, 991.72) * mm, "mid": v(-389.24, 1011.57) * mm, "end": v(-387.06, 1032.05) * mm});
            skArc(sketch, "E279", {"start": v(-387.06, 1032.05) * mm, "mid": v(-387.02, 1064.6) * mm, "end": v(-388.44, 1097.1) * mm});
            skArc(sketch, "E280", {"start": v(-388.44, 1097.1) * mm, "mid": v(-391.15, 1126.45) * mm, "end": v(-395.39, 1155.63) * mm});
            skArc(sketch, "E281", {"start": v(-395.39, 1155.63) * mm, "mid": v(-400.43, 1177) * mm, "end": v(-408.05, 1197.61) * mm});
            skArc(sketch, "E282", {"start": v(-408.05, 1197.61) * mm, "mid": v(-417.19, 1214.75) * mm, "end": v(-428.75, 1230.35) * mm});
            skArc(sketch, "E283", {"start": v(-428.75, 1230.35) * mm, "mid": v(-443.64, 1245.81) * mm, "end": v(-460.14, 1259.55) * mm});
            skArc(sketch, "E284", {"start": v(-460.14, 1259.55) * mm, "mid": v(-492.94, 1280.42) * mm, "end": v(-528.42, 1296.3) * mm});
            skArc(sketch, "E285", {"start": v(-528.42, 1296.3) * mm, "mid": v(-569.56, 1308.77) * mm, "end": v(-611.81, 1316.74) * mm});
            skArc(sketch, "E286", {"start": v(-611.81, 1316.74) * mm, "mid": v(-655.16, 1320.16) * mm, "end": v(-698.62, 1318.95) * mm});
            skArc(sketch, "E287", {"start": v(-698.62, 1318.95) * mm, "mid": v(-738.41, 1312.99) * mm, "end": v(-777.04, 1301.74) * mm});
            skArc(sketch, "E288", {"start": v(-119.08, 517.76) * mm, "mid": v(-116.33, 508.73) * mm, "end": v(-115.46, 499.32) * mm});
            skArc(sketch, "E289", {"start": v(-115.46, 499.32) * mm, "mid": v(-116.19, 487.55) * mm, "end": v(-118.15, 475.91) * mm});
            skArc(sketch, "E290", {"start": v(-118.15, 475.91) * mm, "mid": v(-121.57, 463.5) * mm, "end": v(-126.2, 451.49) * mm});
            skArc(sketch, "E291", {"start": v(-126.2, 451.49) * mm, "mid": v(-131.9, 440.32) * mm, "end": v(-138.74, 429.82) * mm});
            skArc(sketch, "E292", {"start": v(-138.74, 429.82) * mm, "mid": v(-165.03, 412.74) * mm, "end": v(-196.04, 417.46) * mm});
            skArc(sketch, "E293", {"start": v(-196.04, 417.46) * mm, "mid": v(-226.71, 443.68) * mm, "end": v(-245.26, 479.52) * mm});
            skArc(sketch, "E294", {"start": v(-245.26, 479.52) * mm, "mid": v(-258.4, 544.92) * mm, "end": v(-260.1, 611.6) * mm});
            skArc(sketch, "E295", {"start": v(-260.1, 611.6) * mm, "mid": v(-249.7, 672.49) * mm, "end": v(-226.44, 729.71) * mm});
            skArc(sketch, "E296", {"start": v(-226.44, 729.71) * mm, "mid": v(-217.65, 744.73) * mm, "end": v(-207.83, 759.1) * mm});
            skArc(sketch, "E297", {"start": v(-207.83, 759.1) * mm, "mid": v(-202.34, 762.17) * mm, "end": v(-196.42, 760.05) * mm});
            skArc(sketch, "E298", {"start": v(-196.42, 760.05) * mm, "mid": v(-190.04, 752) * mm, "end": v(-185.93, 742.58) * mm});
            skArc(sketch, "E299", {"start": v(-185.93, 742.58) * mm, "mid": v(-175.74, 706.79) * mm, "end": v(-165.93, 670.9) * mm});
            skArc(sketch, "E300", {"start": v(-165.93, 670.9) * mm, "mid": v(-159.58, 647.56) * mm, "end": v(-153.02, 624.29) * mm});
            skArc(sketch, "E301", {"start": v(-153.02, 624.29) * mm, "mid": v(-146.39, 601.5) * mm, "end": v(-139.55, 578.76) * mm});
            skArc(sketch, "E302", {"start": v(-139.55, 578.76) * mm, "mid": v(-133.48, 559.23) * mm, "end": v(-127.24, 539.75) * mm});
            skArc(sketch, "E303", {"start": v(-127.24, 539.75) * mm, "mid": v(-123.38, 528.67) * mm, "end": v(-119.08, 517.76) * mm});
            skArc(sketch, "E304", {"start": v(-53.53, 650.34) * mm, "mid": v(-53.94, 644.5) * mm, "end": v(-55.3, 638.82) * mm});
            skArc(sketch, "E305", {"start": v(-55.3, 638.82) * mm, "mid": v(-57.4, 634.7) * mm, "end": v(-60.72, 631.47) * mm});
            skArc(sketch, "E306", {"start": v(-60.72, 631.47) * mm, "mid": v(-64.62, 629.69) * mm, "end": v(-68.9, 629.42) * mm});
            skArc(sketch, "E307", {"start": v(-68.9, 629.42) * mm, "mid": v(-73.9, 630.58) * mm, "end": v(-78.54, 632.8) * mm});
            skArc(sketch, "E308", {"start": v(-78.54, 632.8) * mm, "mid": v(-84.02, 637.17) * mm, "end": v(-88.27, 642.75) * mm});
            skArc(sketch, "E309", {"start": v(-88.27, 642.75) * mm, "mid": v(-92.74, 651.3) * mm, "end": v(-96.37, 660.23) * mm});
            skArc(sketch, "E310", {"start": v(-96.37, 660.23) * mm, "mid": v(-99.57, 670.84) * mm, "end": v(-101.83, 681.69) * mm});
            skArc(sketch, "E311", {"start": v(-101.83, 681.69) * mm, "mid": v(-103.16, 692.88) * mm, "end": v(-103.56, 704.14) * mm});
            skArc(sketch, "E312", {"start": v(-103.56, 704.14) * mm, "mid": v(-103.28, 719) * mm, "end": v(-102.68, 733.85) * mm});
            skArc(sketch, "E313", {"start": v(-102.68, 733.85) * mm, "mid": v(-101.44, 738.16) * mm, "end": v(-98.44, 741.5) * mm});
            skArc(sketch, "E314", {"start": v(-98.44, 741.5) * mm, "mid": v(-94.96, 742.32) * mm, "end": v(-91.88, 740.5) * mm});
            skArc(sketch, "E315", {"start": v(-91.88, 740.5) * mm, "mid": v(-85.01, 731.24) * mm, "end": v(-78.54, 721.7) * mm});
            skArc(sketch, "E316", {"start": v(-78.54, 721.7) * mm, "mid": v(-73.53, 713.34) * mm, "end": v(-69.09, 704.67) * mm});
            skArc(sketch, "E317", {"start": v(-69.09, 704.67) * mm, "mid": v(-64.81, 694.95) * mm, "end": v(-61.04, 685.02) * mm});
            skArc(sketch, "E318", {"start": v(-61.04, 685.02) * mm, "mid": v(-57.98, 675.48) * mm, "end": v(-55.42, 665.8) * mm});
            skArc(sketch, "E319", {"start": v(-55.42, 665.8) * mm, "mid": v(-54.05, 658.13) * mm, "end": v(-53.53, 650.34) * mm});
            skLineSegment(sketch, "E320", {"start": v(156.15, 377.57) * mm, "end": v(233.07, 312.84) * mm});
            skLineSegment(sketch, "E321", {"start": v(233.07, 312.84) * mm, "end": v(293.16, 369.3) * mm});
            skArc(sketch, "E322", {"start": v(293.16, 369.3) * mm, "mid": v(313.54, 388.26) * mm, "end": v(334.09, 407.03) * mm});
            skArc(sketch, "E323", {"start": v(334.09, 407.03) * mm, "mid": v(339.45, 410.44) * mm, "end": v(345.63, 411.87) * mm});
            skArc(sketch, "E324", {"start": v(345.63, 411.87) * mm, "mid": v(350.03, 410.36) * mm, "end": v(352.09, 406.2) * mm});
            skArc(sketch, "E325", {"start": v(352.09, 406.2) * mm, "mid": v(352.96, 389.5) * mm, "end": v(353.26, 372.78) * mm});
            skArc(sketch, "E326", {"start": v(353.26, 372.78) * mm, "mid": v(352, 360.27) * mm, "end": v(348.32, 348.26) * mm});
            skArc(sketch, "E327", {"start": v(348.32, 348.26) * mm, "mid": v(341.06, 332.77) * mm, "end": v(332.57, 317.92) * mm});
            skArc(sketch, "E328", {"start": v(332.57, 317.92) * mm, "mid": v(321.76, 302.05) * mm, "end": v(309.78, 287.05) * mm});
            skArc(sketch, "E329", {"start": v(309.78, 287.05) * mm, "mid": v(296.83, 273.2) * mm, "end": v(282.83, 260.4) * mm});
            skArc(sketch, "E330", {"start": v(282.83, 260.4) * mm, "mid": v(248.92, 229.97) * mm, "end": v(216.93, 197.53) * mm});
            skArc(sketch, "E331", {"start": v(216.93, 197.53) * mm, "mid": v(190.53, 166.52) * mm, "end": v(166.86, 133.37) * mm});
            skArc(sketch, "E332", {"start": v(166.86, 133.37) * mm, "mid": v(149.44, 103.46) * mm, "end": v(135.07, 71.97) * mm});
            skArc(sketch, "E333", {"start": v(135.07, 71.97) * mm, "mid": v(127.28, 45.25) * mm, "end": v(124.66, 17.54) * mm});
            skArc(sketch, "E334", {"start": v(124.66, 17.54) * mm, "mid": v(124.24, 6.43) * mm, "end": v(123, -4.61) * mm});
            skArc(sketch, "E335", {"start": v(123, -4.61) * mm, "mid": v(121.02, -14.1) * mm, "end": v(118, -23.31) * mm});
            skArc(sketch, "E336", {"start": v(118, -23.31) * mm, "mid": v(114.8, -29.97) * mm, "end": v(110.66, -36.1) * mm});
            skArc(sketch, "E337", {"start": v(110.66, -36.1) * mm, "mid": v(106.8, -39.2) * mm, "end": v(101.97, -40.3) * mm});
            skArc(sketch, "E338", {"start": v(101.97, -40.3) * mm, "mid": v(88.59, -36.84) * mm, "end": v(78.57, -27.31) * mm});
            skArc(sketch, "E339", {"start": v(78.57, -27.31) * mm, "mid": v(68.72, -8.41) * mm, "end": v(61.85, 11.76) * mm});
            skArc(sketch, "E340", {"start": v(61.85, 11.76) * mm, "mid": v(55.22, 43.54) * mm, "end": v(51.55, 75.8) * mm});
            skArc(sketch, "E341", {"start": v(51.55, 75.8) * mm, "mid": v(49.23, 121.73) * mm, "end": v(48.46, 167.72) * mm});
            skArc(sketch, "E342", {"start": v(48.46, 167.72) * mm, "mid": v(48.14, 208.12) * mm, "end": v(47.18, 248.5) * mm});
            skArc(sketch, "E343", {"start": v(47.18, 248.5) * mm, "mid": v(45.09, 262.38) * mm, "end": v(39.8, 275.38) * mm});
            skArc(sketch, "E344", {"start": v(39.8, 275.38) * mm, "mid": v(32.73, 282.54) * mm, "end": v(22.97, 284.95) * mm});
            skArc(sketch, "E345", {"start": v(22.97, 284.95) * mm, "mid": v(4.6, 283.38) * mm, "end": v(-13.49, 279.85) * mm});
            skArc(sketch, "E346", {"start": v(-13.49, 279.85) * mm, "mid": v(-37.67, 275.92) * mm, "end": v(-62.17, 276.12) * mm});
            skArc(sketch, "E347", {"start": v(-62.17, 276.12) * mm, "mid": v(-78.5, 281.56) * mm, "end": v(-90.72, 293.67) * mm});
            skArc(sketch, "E348", {"start": v(-90.72, 293.67) * mm, "mid": v(-97.34, 311.07) * mm, "end": v(-96.72, 329.67) * mm});
            skArc(sketch, "E349", {"start": v(-96.72, 329.67) * mm, "mid": v(-88.67, 356.08) * mm, "end": v(-77.25, 381.21) * mm});
            skArc(sketch, "E350", {"start": v(-77.25, 381.21) * mm, "mid": v(-59.7, 405.8) * mm, "end": v(-36.48, 425.1) * mm});
            skArc(sketch, "E351", {"start": v(-36.48, 425.1) * mm, "mid": v(-10.01, 436.91) * mm, "end": v(18.72, 440.65) * mm});
            skArc(sketch, "E352", {"start": v(18.72, 440.65) * mm, "mid": v(52.71, 436.29) * mm, "end": v(84.88, 424.46) * mm});
            skArc(sketch, "E353", {"start": v(84.88, 424.46) * mm, "mid": v(121.9, 403.1) * mm, "end": v(156.15, 377.57) * mm});
            skArc(sketch, "E354", {"start": v(-251.26, 340.7) * mm, "mid": v(-241.95, 339.86) * mm, "end": v(-232.92, 337.4) * mm});
            skArc(sketch, "E355", {"start": v(-232.92, 337.4) * mm, "mid": v(-225.07, 333.5) * mm, "end": v(-218.24, 328) * mm});
            skArc(sketch, "E356", {"start": v(-218.24, 328) * mm, "mid": v(-212.75, 321.16) * mm, "end": v(-208.84, 313.32) * mm});
            skArc(sketch, "E357", {"start": v(-208.84, 313.32) * mm, "mid": v(-206.37, 304.3) * mm, "end": v(-205.54, 294.97) * mm});
            skArc(sketch, "E358", {"start": v(-205.54, 294.97) * mm, "mid": v(-205.06, 285.2) * mm, "end": v(-203.6, 275.54) * mm});
            skArc(sketch, "E359", {"start": v(-203.6, 275.54) * mm, "mid": v(-201.1, 265.13) * mm, "end": v(-197.8, 254.94) * mm});
            skArc(sketch, "E360", {"start": v(-197.8, 254.94) * mm, "mid": v(-193.92, 245.46) * mm, "end": v(-189.3, 236.3) * mm});
            skArc(sketch, "E361", {"start": v(-189.3, 236.3) * mm, "mid": v(-184.72, 229.26) * mm, "end": v(-179.2, 222.9) * mm});
            skArc(sketch, "E362", {"start": v(-179.2, 222.9) * mm, "mid": v(-173.38, 215.62) * mm, "end": v(-169.3, 207.23) * mm});
            skArc(sketch, "E363", {"start": v(-169.3, 207.23) * mm, "mid": v(-166.63, 197.2) * mm, "end": v(-165.6, 186.88) * mm});
            skArc(sketch, "E364", {"start": v(-165.6, 186.88) * mm, "mid": v(-166.18, 174.18) * mm, "end": v(-168.34, 161.66) * mm});
            skArc(sketch, "E365", {"start": v(-168.34, 161.66) * mm, "mid": v(-172.5, 146.38) * mm, "end": v(-177.63, 131.4) * mm});
            skArc(sketch, "E366", {"start": v(-177.63, 131.4) * mm, "mid": v(-192.06, 96.43) * mm, "end": v(-208.42, 62.33) * mm});
            skArc(sketch, "E367", {"start": v(-208.42, 62.33) * mm, "mid": v(-218.8, 52.1) * mm, "end": v(-233.24, 50.07) * mm});
            skArc(sketch, "E368", {"start": v(-233.24, 50.07) * mm, "mid": v(-246.01, 57.02) * mm, "end": v(-252.1, 70.22) * mm});
            skArc(sketch, "E369", {"start": v(-252.1, 70.22) * mm, "mid": v(-255.28, 107.84) * mm, "end": v(-256.34, 145.58) * mm});
            skArc(sketch, "E370", {"start": v(-256.34, 145.58) * mm, "mid": v(-258.15, 185.21) * mm, "end": v(-263.56, 224.51) * mm});
            skArc(sketch, "E371", {"start": v(-263.56, 224.51) * mm, "mid": v(-272, 252.55) * mm, "end": v(-286.37, 278.08) * mm});
            skArc(sketch, "E372", {"start": v(-286.37, 278.08) * mm, "mid": v(-302.16, 293.55) * mm, "end": v(-322.25, 302.77) * mm});
            skArc(sketch, "E373", {"start": v(-322.25, 302.77) * mm, "mid": v(-345.03, 305.1) * mm, "end": v(-367.43, 300.31) * mm});
            skArc(sketch, "E374", {"start": v(-367.43, 300.31) * mm, "mid": v(-380.83, 296.73) * mm, "end": v(-394.7, 296.01) * mm});
            skArc(sketch, "E375", {"start": v(-394.7, 296.01) * mm, "mid": v(-403.02, 299.42) * mm, "end": v(-407.42, 307.26) * mm});
            skArc(sketch, "E376", {"start": v(-407.42, 307.26) * mm, "mid": v(-407.28, 319.55) * mm, "end": v(-402.63, 330.93) * mm});
            skArc(sketch, "E377", {"start": v(-402.63, 330.93) * mm, "mid": v(-391.24, 346.6) * mm, "end": v(-378.26, 361.01) * mm});
            skArc(sketch, "E378", {"start": v(-378.26, 361.01) * mm, "mid": v(-371.15, 367.34) * mm, "end": v(-363.34, 372.78) * mm});
            skArc(sketch, "E379", {"start": v(-363.34, 372.78) * mm, "mid": v(-356.47, 375.98) * mm, "end": v(-349.05, 377.52) * mm});
            skArc(sketch, "E380", {"start": v(-349.05, 377.52) * mm, "mid": v(-342.08, 377.24) * mm, "end": v(-335.41, 375.17) * mm});
            skArc(sketch, "E381", {"start": v(-335.41, 375.17) * mm, "mid": v(-328.5, 371.21) * mm, "end": v(-322.38, 366.1) * mm});
            skArc(sketch, "E382", {"start": v(-322.38, 366.1) * mm, "mid": v(-316.22, 360.76) * mm, "end": v(-309.35, 356.36) * mm});
            skArc(sketch, "E383", {"start": v(-309.35, 356.36) * mm, "mid": v(-300.34, 351.9) * mm, "end": v(-291.02, 348.15) * mm});
            skArc(sketch, "E384", {"start": v(-291.02, 348.15) * mm, "mid": v(-280.93, 344.97) * mm, "end": v(-270.63, 342.56) * mm});
            skArc(sketch, "E385", {"start": v(-270.63, 342.56) * mm, "mid": v(-261, 341.16) * mm, "end": v(-251.26, 340.7) * mm});
            skArc(sketch, "E386", {"start": v(-374.62, 67.72) * mm, "mid": v(-368.12, 52.68) * mm, "end": v(-366.22, 36.42) * mm});
            skArc(sketch, "E387", {"start": v(-366.22, 36.42) * mm, "mid": v(-368.57, 17.6) * mm, "end": v(-374.43, -0.43) * mm});
            skArc(sketch, "E388", {"start": v(-374.43, -0.43) * mm, "mid": v(-383.23, -16.15) * mm, "end": v(-395, -29.78) * mm});
            skArc(sketch, "E389", {"start": v(-395, -29.78) * mm, "mid": v(-407.21, -37.58) * mm, "end": v(-421.44, -40.3) * mm});
            skArc(sketch, "E390", {"start": v(-421.44, -40.3) * mm, "mid": v(-443.66, -34.41) * mm, "end": v(-460.04, -18.29) * mm});
            skArc(sketch, "E391", {"start": v(-460.04, -18.29) * mm, "mid": v(-473.75, 11.2) * mm, "end": v(-481.42, 42.8) * mm});
            skArc(sketch, "E392", {"start": v(-481.42, 42.8) * mm, "mid": v(-483.92, 82.76) * mm, "end": v(-480.25, 122.64) * mm});
            skArc(sketch, "E393", {"start": v(-480.25, 122.64) * mm, "mid": v(-470.52, 160.53) * mm, "end": v(-454.7, 196.31) * mm});
            skArc(sketch, "E394", {"start": v(-454.7, 196.31) * mm, "mid": v(-444.83, 213.93) * mm, "end": v(-434.58, 231.33) * mm});
            skArc(sketch, "E395", {"start": v(-434.58, 231.33) * mm, "mid": v(-430.91, 234.16) * mm, "end": v(-426.29, 233.77) * mm});
            skArc(sketch, "E396", {"start": v(-426.29, 233.77) * mm, "mid": v(-421.87, 230.22) * mm, "end": v(-419.4, 225.11) * mm});
            skArc(sketch, "E397", {"start": v(-419.4, 225.11) * mm, "mid": v(-413.54, 199.27) * mm, "end": v(-407.94, 173.38) * mm});
            skArc(sketch, "E398", {"start": v(-407.94, 173.38) * mm, "mid": v(-404.36, 157.32) * mm, "end": v(-400.4, 141.36) * mm});
            skArc(sketch, "E399", {"start": v(-400.4, 141.36) * mm, "mid": v(-396.07, 125.62) * mm, "end": v(-391.35, 110) * mm});
            skArc(sketch, "E400", {"start": v(-391.35, 110) * mm, "mid": v(-386.92, 96.54) * mm, "end": v(-382.17, 83.2) * mm});
            skArc(sketch, "E401", {"start": v(-382.17, 83.2) * mm, "mid": v(-378.78, 75.27) * mm, "end": v(-374.62, 67.72) * mm});
            skArc(sketch, "E402", {"start": v(-307.14, 161.4) * mm, "mid": v(-307.6, 151.88) * mm, "end": v(-308.96, 142.46) * mm});
            skArc(sketch, "E403", {"start": v(-308.96, 142.46) * mm, "mid": v(-311.09, 135.47) * mm, "end": v(-314.6, 129.07) * mm});
            skArc(sketch, "E404", {"start": v(-314.6, 129.07) * mm, "mid": v(-318.25, 125.43) * mm, "end": v(-322.94, 123.3) * mm});
            skArc(sketch, "E405", {"start": v(-322.94, 123.3) * mm, "mid": v(-327.9, 123.08) * mm, "end": v(-332.54, 124.8) * mm});
            skArc(sketch, "E406", {"start": v(-332.54, 124.8) * mm, "mid": v(-337.8, 128.71) * mm, "end": v(-342.27, 133.49) * mm});
            skArc(sketch, "E407", {"start": v(-342.27, 133.49) * mm, "mid": v(-346.73, 139.84) * mm, "end": v(-350.48, 146.63) * mm});
            skArc(sketch, "E408", {"start": v(-350.48, 146.63) * mm, "mid": v(-353.66, 154.14) * mm, "end": v(-356.06, 161.93) * mm});
            skArc(sketch, "E409", {"start": v(-356.06, 161.93) * mm, "mid": v(-357.47, 169.45) * mm, "end": v(-357.94, 177.1) * mm});
            skArc(sketch, "E410", {"start": v(-357.94, 177.1) * mm, "mid": v(-357.47, 184.15) * mm, "end": v(-356.04, 191.08) * mm});
            skArc(sketch, "E411", {"start": v(-356.04, 191.08) * mm, "mid": v(-353.76, 197.25) * mm, "end": v(-350.48, 202.94) * mm});
            skArc(sketch, "E412", {"start": v(-350.48, 202.94) * mm, "mid": v(-346.75, 207.32) * mm, "end": v(-342.23, 210.87) * mm});
            skArc(sketch, "E413", {"start": v(-342.23, 210.87) * mm, "mid": v(-337.59, 212.97) * mm, "end": v(-332.54, 213.7) * mm});
            skArc(sketch, "E414", {"start": v(-332.54, 213.7) * mm, "mid": v(-327.3, 212.67) * mm, "end": v(-322.84, 209.75) * mm});
            skArc(sketch, "E415", {"start": v(-322.84, 209.75) * mm, "mid": v(-318.23, 204.4) * mm, "end": v(-314.6, 198.33) * mm});
            skArc(sketch, "E416", {"start": v(-314.6, 198.33) * mm, "mid": v(-311.25, 190.06) * mm, "end": v(-309.01, 181.41) * mm});
            skArc(sketch, "E417", {"start": v(-309.01, 181.41) * mm, "mid": v(-307.61, 171.45) * mm, "end": v(-307.14, 161.4) * mm});
            skArc(sketch, "E418", {"start": v(315.03, -87.97) * mm, "mid": v(309.8, -127.7) * mm, "end": v(304.04, -167.34) * mm});
            skArc(sketch, "E419", {"start": v(304.04, -167.34) * mm, "mid": v(300.52, -181.72) * mm, "end": v(294.5, -195.25) * mm});
            skArc(sketch, "E420", {"start": v(294.5, -195.25) * mm, "mid": v(288.6, -200.28) * mm, "end": v(280.85, -200.2) * mm});
            skArc(sketch, "E421", {"start": v(280.85, -200.2) * mm, "mid": v(269.81, -194.53) * mm, "end": v(260.18, -186.72) * mm});
            skArc(sketch, "E422", {"start": v(260.18, -186.72) * mm, "mid": v(251.55, -176.57) * mm, "end": v(244.68, -165.17) * mm});
            skArc(sketch, "E423", {"start": v(244.68, -165.17) * mm, "mid": v(236.55, -147.64) * mm, "end": v(229.4, -129.7) * mm});
            skArc(sketch, "E424", {"start": v(229.4, -129.7) * mm, "mid": v(222.44, -109.01) * mm, "end": v(216.6, -87.99) * mm});
            skArc(sketch, "E425", {"start": v(216.6, -87.99) * mm, "mid": v(211.97, -66.96) * mm, "end": v(208.52, -45.71) * mm});
            skArc(sketch, "E426", {"start": v(208.52, -45.71) * mm, "mid": v(205.65, -17.83) * mm, "end": v(204.5, 10.17) * mm});
            skArc(sketch, "E427", {"start": v(204.5, 10.17) * mm, "mid": v(205.67, 32.1) * mm, "end": v(209.59, 53.7) * mm});
            skArc(sketch, "E428", {"start": v(209.59, 53.7) * mm, "mid": v(216.19, 74.63) * mm, "end": v(225.37, 94.54) * mm});
            skArc(sketch, "E429", {"start": v(225.37, 94.54) * mm, "mid": v(239.4, 118.7) * mm, "end": v(254.92, 141.93) * mm});
            skLineSegment(sketch, "E430", {"start": v(254.92, 141.93) * mm, "end": v(315.16, 226.4) * mm});
            skLineSegment(sketch, "E431", {"start": v(315.16, 226.4) * mm, "end": v(323.61, 137.5) * mm});
            skArc(sketch, "E432", {"start": v(323.61, 137.5) * mm, "mid": v(325.17, 115.72) * mm, "end": v(325.7, 93.9) * mm});
            skArc(sketch, "E433", {"start": v(325.7, 93.9) * mm, "mid": v(325.42, 64.24) * mm, "end": v(324.58, 34.6) * mm});
            skArc(sketch, "E434", {"start": v(324.58, 34.6) * mm, "mid": v(323.06, 2.7) * mm, "end": v(320.94, -29.17) * mm});
            skArc(sketch, "E435", {"start": v(320.94, -29.17) * mm, "mid": v(318.34, -58.6) * mm, "end": v(315.03, -87.97) * mm});
            skArc(sketch, "E436", {"start": v(-56.86, 64.13) * mm, "mid": v(-56.98, 14.64) * mm, "end": v(-55.11, -34.82) * mm});
            skArc(sketch, "E437", {"start": v(-55.11, -34.82) * mm, "mid": v(-50.57, -60.24) * mm, "end": v(-40.16, -83.87) * mm});
            skArc(sketch, "E438", {"start": v(-40.16, -83.87) * mm, "mid": v(-26.54, -99.26) * mm, "end": v(-8.18, -108.47) * mm});
            skArc(sketch, "E439", {"start": v(-8.18, -108.47) * mm, "mid": v(20.61, -114.49) * mm, "end": v(49.95, -116.5) * mm});
            skArc(sketch, "E440", {"start": v(49.95, -116.5) * mm, "mid": v(66.85, -117.08) * mm, "end": v(83.66, -118.8) * mm});
            skArc(sketch, "E441", {"start": v(83.66, -118.8) * mm, "mid": v(95.45, -121.52) * mm, "end": v(106.56, -126.29) * mm});
            skArc(sketch, "E442", {"start": v(106.56, -126.29) * mm, "mid": v(114.04, -131.76) * mm, "end": v(119.79, -139.04) * mm});
            skArc(sketch, "E443", {"start": v(119.79, -139.04) * mm, "mid": v(123.42, -147.64) * mm, "end": v(124.66, -156.89) * mm});
            skArc(sketch, "E444", {"start": v(124.66, -156.89) * mm, "mid": v(127.65, -175.57) * mm, "end": v(136.34, -192.4) * mm});
            skArc(sketch, "E445", {"start": v(136.34, -192.4) * mm, "mid": v(155.97, -216.96) * mm, "end": v(177.44, -239.95) * mm});
            skArc(sketch, "E446", {"start": v(177.44, -239.95) * mm, "mid": v(200.72, -261.32) * mm, "end": v(225.59, -280.82) * mm});
            skArc(sketch, "E447", {"start": v(225.59, -280.82) * mm, "mid": v(243.03, -289.87) * mm, "end": v(262.36, -293.46) * mm});
            skArc(sketch, "E448", {"start": v(262.36, -293.46) * mm, "mid": v(268.59, -292.95) * mm, "end": v(274.53, -291.01) * mm});
            skArc(sketch, "E449", {"start": v(274.53, -291.01) * mm, "mid": v(284.16, -286.25) * mm, "end": v(293.53, -281) * mm});
            skArc(sketch, "E450", {"start": v(293.53, -281) * mm, "mid": v(304.36, -274.18) * mm, "end": v(314.82, -266.81) * mm});
            skArc(sketch, "E451", {"start": v(314.82, -266.81) * mm, "mid": v(325.41, -258.56) * mm, "end": v(335.63, -249.86) * mm});
            skArc(sketch, "E452", {"start": v(335.63, -249.86) * mm, "mid": v(348.53, -240.48) * mm, "end": v(363.03, -233.82) * mm});
            skArc(sketch, "E453", {"start": v(363.03, -233.82) * mm, "mid": v(371.76, -234.73) * mm, "end": v(376.7, -242) * mm});
            skArc(sketch, "E454", {"start": v(376.7, -242) * mm, "mid": v(378.93, -263.4) * mm, "end": v(378.7, -284.93) * mm});
            skArc(sketch, "E455", {"start": v(378.7, -284.93) * mm, "mid": v(373.12, -364.47) * mm, "end": v(367.2, -443.99) * mm});
            skArc(sketch, "E456", {"start": v(367.2, -443.99) * mm, "mid": v(363.4, -490.95) * mm, "end": v(359.21, -537.89) * mm});
            skArc(sketch, "E457", {"start": v(359.21, -537.89) * mm, "mid": v(355.02, -580.27) * mm, "end": v(350.37, -622.61) * mm});
            skArc(sketch, "E458", {"start": v(350.37, -622.61) * mm, "mid": v(346.14, -658) * mm, "end": v(341.65, -693.37) * mm});
            skArc(sketch, "E459", {"start": v(341.65, -693.37) * mm, "mid": v(339.35, -705.38) * mm, "end": v(335.65, -717.04) * mm});
            skArc(sketch, "E460", {"start": v(335.65, -717.04) * mm, "mid": v(327.53, -732.96) * mm, "end": v(316.26, -746.83) * mm});
            skArc(sketch, "E461", {"start": v(316.26, -746.83) * mm, "mid": v(306.34, -750.96) * mm, "end": v(296.38, -746.91) * mm});
            skArc(sketch, "E462", {"start": v(296.38, -746.91) * mm, "mid": v(285.8, -732.72) * mm, "end": v(280.03, -715.99) * mm});
            skArc(sketch, "E463", {"start": v(280.03, -715.99) * mm, "mid": v(275.77, -686.23) * mm, "end": v(273.63, -656.26) * mm});
            skArc(sketch, "E464", {"start": v(273.63, -656.26) * mm, "mid": v(270.2, -566.67) * mm, "end": v(266.3, -477.1) * mm});
            skArc(sketch, "E465", {"start": v(266.3, -477.1) * mm, "mid": v(263.61, -454.42) * mm, "end": v(257.67, -432.38) * mm});
            skArc(sketch, "E466", {"start": v(257.67, -432.38) * mm, "mid": v(249.37, -419.37) * mm, "end": v(236.13, -411.45) * mm});
            skArc(sketch, "E467", {"start": v(236.13, -411.45) * mm, "mid": v(210.54, -404.78) * mm, "end": v(184.4, -400.84) * mm});
            skArc(sketch, "E468", {"start": v(184.4, -400.84) * mm, "mid": v(165.81, -398.3) * mm, "end": v(147.5, -394.29) * mm});
            skArc(sketch, "E469", {"start": v(147.5, -394.29) * mm, "mid": v(133.46, -389.43) * mm, "end": v(120.37, -382.44) * mm});
            skArc(sketch, "E470", {"start": v(120.37, -382.44) * mm, "mid": v(110.27, -374.51) * mm, "end": v(101.88, -364.79) * mm});
            skArc(sketch, "E471", {"start": v(101.88, -364.79) * mm, "mid": v(95.28, -353.4) * mm, "end": v(90.83, -341.02) * mm});
            skArc(sketch, "E472", {"start": v(90.83, -341.02) * mm, "mid": v(87.59, -331.23) * mm, "end": v(83.13, -321.95) * mm});
            skArc(sketch, "E473", {"start": v(83.13, -321.95) * mm, "mid": v(77.88, -314.24) * mm, "end": v(71.4, -307.54) * mm});
            skArc(sketch, "E474", {"start": v(71.4, -307.54) * mm, "mid": v(64.89, -303.01) * mm, "end": v(57.58, -299.95) * mm});
            skArc(sketch, "E475", {"start": v(57.58, -299.95) * mm, "mid": v(50.66, -299) * mm, "end": v(43.78, -300.18) * mm});
            skArc(sketch, "E476", {"start": v(43.78, -300.18) * mm, "mid": v(34.68, -305.59) * mm, "end": v(28.63, -314.28) * mm});
            skArc(sketch, "E477", {"start": v(28.63, -314.28) * mm, "mid": v(22.63, -331) * mm, "end": v(18.35, -348.24) * mm});
            skArc(sketch, "E478", {"start": v(18.35, -348.24) * mm, "mid": v(14.24, -374.05) * mm, "end": v(11.93, -400.08) * mm});
            skArc(sketch, "E479", {"start": v(11.93, -400.08) * mm, "mid": v(10.41, -437.18) * mm, "end": v(9.83, -474.3) * mm});
            skArc(sketch, "E480", {"start": v(9.83, -474.3) * mm, "mid": v(8.07, -529.84) * mm, "end": v(3.15, -585.2) * mm});
            skArc(sketch, "E481", {"start": v(3.15, -585.2) * mm, "mid": v(-4.47, -629.96) * mm, "end": v(-16.68, -673.7) * mm});
            skArc(sketch, "E482", {"start": v(-16.68, -673.7) * mm, "mid": v(-29.37, -704.08) * mm, "end": v(-46.3, -732.34) * mm});
            skArc(sketch, "E483", {"start": v(-46.3, -732.34) * mm, "mid": v(-62.4, -746.43) * mm, "end": v(-83.19, -751.5) * mm});
            skArc(sketch, "E484", {"start": v(-83.19, -751.5) * mm, "mid": v(-91.45, -748.49) * mm, "end": v(-95.82, -740.86) * mm});
            skArc(sketch, "E485", {"start": v(-95.82, -740.86) * mm, "mid": v(-99.03, -718.06) * mm, "end": v(-100.83, -695.1) * mm});
            skArc(sketch, "E486", {"start": v(-100.83, -695.1) * mm, "mid": v(-101.71, -659.15) * mm, "end": v(-100.96, -623.2) * mm});
            skArc(sketch, "E487", {"start": v(-100.96, -623.2) * mm, "mid": v(-98.15, -567.55) * mm, "end": v(-94.6, -511.95) * mm});
            skArc(sketch, "E488", {"start": v(-94.6, -511.95) * mm, "mid": v(-91.28, -458.78) * mm, "end": v(-88.77, -405.57) * mm});
            skArc(sketch, "E489", {"start": v(-88.77, -405.57) * mm, "mid": v(-88, -367) * mm, "end": v(-88.76, -328.43) * mm});
            skArc(sketch, "E490", {"start": v(-88.76, -328.43) * mm, "mid": v(-90.4, -301.04) * mm, "end": v(-93.17, -273.73) * mm});
            skArc(sketch, "E491", {"start": v(-93.17, -273.73) * mm, "mid": v(-96.87, -263.44) * mm, "end": v(-104.67, -255.76) * mm});
            skArc(sketch, "E492", {"start": v(-104.67, -255.76) * mm, "mid": v(-123.62, -250.02) * mm, "end": v(-142.92, -254.42) * mm});
            skArc(sketch, "E493", {"start": v(-142.92, -254.42) * mm, "mid": v(-161.63, -268.53) * mm, "end": v(-174.83, -287.88) * mm});
            skArc(sketch, "E494", {"start": v(-174.83, -287.88) * mm, "mid": v(-189.32, -325.6) * mm, "end": v(-198.44, -364.95) * mm});
            skArc(sketch, "E495", {"start": v(-198.44, -364.95) * mm, "mid": v(-206.9, -426.2) * mm, "end": v(-212.84, -487.74) * mm});
            skArc(sketch, "E496", {"start": v(-212.84, -487.74) * mm, "mid": v(-217.29, -538.56) * mm, "end": v(-222.93, -589.26) * mm});
            skArc(sketch, "E497", {"start": v(-222.93, -589.26) * mm, "mid": v(-228.34, -622.36) * mm, "end": v(-236.32, -654.94) * mm});
            skArc(sketch, "E498", {"start": v(-236.32, -654.94) * mm, "mid": v(-244.9, -679.43) * mm, "end": v(-256.25, -702.77) * mm});
            skArc(sketch, "E499", {"start": v(-256.25, -702.77) * mm, "mid": v(-270.06, -724.26) * mm, "end": v(-286.35, -743.93) * mm});
            skLineSegment(sketch, "E500", {"start": v(-286.35, -743.93) * mm, "end": v(-345.24, -806.84) * mm});
            skLineSegment(sketch, "E501", {"start": v(-345.24, -806.84) * mm, "end": v(-357.94, -607.72) * mm});
            skArc(sketch, "E502", {"start": v(-357.94, -607.72) * mm, "mid": v(-361.98, -550.28) * mm, "end": v(-366.74, -492.88) * mm});
            skArc(sketch, "E503", {"start": v(-366.74, -492.88) * mm, "mid": v(-370.43, -467.2) * mm, "end": v(-376.85, -442.04) * mm});
            skArc(sketch, "E504", {"start": v(-376.85, -442.04) * mm, "mid": v(-383.37, -428.68) * mm, "end": v(-393.55, -417.86) * mm});
            skArc(sketch, "E505", {"start": v(-393.55, -417.86) * mm, "mid": v(-406.15, -410.98) * mm, "end": v(-420.3, -408.6) * mm});
            skArc(sketch, "E506", {"start": v(-420.3, -408.6) * mm, "mid": v(-432.92, -410.04) * mm, "end": v(-444.88, -414.28) * mm});
            skArc(sketch, "E507", {"start": v(-444.88, -414.28) * mm, "mid": v(-455.2, -421.02) * mm, "end": v(-463.54, -430.07) * mm});
            skArc(sketch, "E508", {"start": v(-463.54, -430.07) * mm, "mid": v(-471.93, -444.02) * mm, "end": v(-478, -459.11) * mm});
            skArc(sketch, "E509", {"start": v(-478, -459.11) * mm, "mid": v(-484.74, -482.65) * mm, "end": v(-490.31, -506.5) * mm});
            skArc(sketch, "E510", {"start": v(-490.31, -506.5) * mm, "mid": v(-501.44, -549.2) * mm, "end": v(-516.77, -590.6) * mm});
            skArc(sketch, "E511", {"start": v(-516.77, -590.6) * mm, "mid": v(-536.77, -632.15) * mm, "end": v(-560.33, -671.79) * mm});
            skArc(sketch, "E512", {"start": v(-560.33, -671.79) * mm, "mid": v(-583.5, -703.88) * mm, "end": v(-609.48, -733.76) * mm});
            skArc(sketch, "E513", {"start": v(-609.48, -733.76) * mm, "mid": v(-628.36, -746.88) * mm, "end": v(-650.88, -751.5) * mm});
            skArc(sketch, "E514", {"start": v(-650.88, -751.5) * mm, "mid": v(-686.46, -740.22) * mm, "end": v(-709.02, -710.5) * mm});
            skArc(sketch, "E515", {"start": v(-709.02, -710.5) * mm, "mid": v(-727.13, -646.72) * mm, "end": v(-736.73, -581.1) * mm});
            skArc(sketch, "E516", {"start": v(-736.73, -581.1) * mm, "mid": v(-738.6, -500.18) * mm, "end": v(-731.32, -419.56) * mm});
            skArc(sketch, "E517", {"start": v(-731.32, -419.56) * mm, "mid": v(-715.13, -345.93) * mm, "end": v(-688.84, -275.28) * mm});
            skArc(sketch, "E518", {"start": v(-688.84, -275.28) * mm, "mid": v(-668.01, -235.76) * mm, "end": v(-642.68, -198.96) * mm});
            skArc(sketch, "E519", {"start": v(-642.68, -198.96) * mm, "mid": v(-615.28, -168.95) * mm, "end": v(-583.55, -143.57) * mm});
            skArc(sketch, "E520", {"start": v(-583.55, -143.57) * mm, "mid": v(-555.95, -128.93) * mm, "end": v(-525.83, -120.6) * mm});
            skArc(sketch, "E521", {"start": v(-525.83, -120.6) * mm, "mid": v(-502.16, -122.4) * mm, "end": v(-481.9, -134.79) * mm});
            skArc(sketch, "E522", {"start": v(-481.9, -134.79) * mm, "mid": v(-471.98, -150.33) * mm, "end": v(-469.52, -168.6) * mm});
            skArc(sketch, "E523", {"start": v(-469.52, -168.6) * mm, "mid": v(-473.93, -192.57) * mm, "end": v(-482.94, -215.2) * mm});
            skArc(sketch, "E524", {"start": v(-482.94, -215.2) * mm, "mid": v(-496.61, -236.52) * mm, "end": v(-514.01, -254.92) * mm});
            skArc(sketch, "E525", {"start": v(-514.01, -254.92) * mm, "mid": v(-531.33, -265.3) * mm, "end": v(-551.2, -268.9) * mm});
            skArc(sketch, "E526", {"start": v(-551.2, -268.9) * mm, "mid": v(-558.95, -269.72) * mm, "end": v(-566.36, -272.1) * mm});
            skArc(sketch, "E527", {"start": v(-566.36, -272.1) * mm, "mid": v(-572.4, -275.83) * mm, "end": v(-577.19, -281.05) * mm});
            skArc(sketch, "E528", {"start": v(-577.19, -281.05) * mm, "mid": v(-580.7, -287.78) * mm, "end": v(-582.47, -295.17) * mm});
            skArc(sketch, "E529", {"start": v(-582.47, -295.17) * mm, "mid": v(-582.8, -304.14) * mm, "end": v(-581.77, -313.07) * mm});
            skArc(sketch, "E530", {"start": v(-581.77, -313.07) * mm, "mid": v(-567.46, -341.2) * mm, "end": v(-540.38, -357.41) * mm});
            skArc(sketch, "E531", {"start": v(-540.38, -357.41) * mm, "mid": v(-504.59, -359.58) * mm, "end": v(-470.75, -347.72) * mm});
            skArc(sketch, "E532", {"start": v(-470.75, -347.72) * mm, "mid": v(-433.7, -318.8) * mm, "end": v(-405.08, -281.51) * mm});
            skArc(sketch, "E533", {"start": v(-405.08, -281.51) * mm, "mid": v(-389.32, -240.86) * mm, "end": v(-386.94, -197.32) * mm});
            skArc(sketch, "E534", {"start": v(-386.94, -197.32) * mm, "mid": v(-386.67, -166.08) * mm, "end": v(-379.45, -135.69) * mm});
            skArc(sketch, "E535", {"start": v(-379.45, -135.69) * mm, "mid": v(-365.05, -103.99) * mm, "end": v(-345.7, -75.04) * mm});
            skArc(sketch, "E536", {"start": v(-345.7, -75.04) * mm, "mid": v(-322.72, -50.6) * mm, "end": v(-295.95, -30.4) * mm});
            skArc(sketch, "E537", {"start": v(-295.95, -30.4) * mm, "mid": v(-270.22, -18.86) * mm, "end": v(-242.3, -14.9) * mm});
            skArc(sketch, "E538", {"start": v(-242.3, -14.9) * mm, "mid": v(-223.93, -12.4) * mm, "end": v(-206.92, -5.04) * mm});
            skArc(sketch, "E539", {"start": v(-206.92, -5.04) * mm, "mid": v(-189.92, 7.51) * mm, "end": v(-175.51, 22.98) * mm});
            skArc(sketch, "E540", {"start": v(-175.51, 22.98) * mm, "mid": v(-159.7, 46.34) * mm, "end": v(-146.9, 71.47) * mm});
            skArc(sketch, "E541", {"start": v(-146.9, 71.47) * mm, "mid": v(-132.43, 107.32) * mm, "end": v(-119.75, 143.84) * mm});
            skArc(sketch, "E542", {"start": v(-119.75, 143.84) * mm, "mid": v(-110.9, 164.49) * mm, "end": v(-98.3, 183.08) * mm});
            skArc(sketch, "E543", {"start": v(-98.3, 183.08) * mm, "mid": v(-87.4, 188.13) * mm, "end": v(-76.63, 182.83) * mm});
            skArc(sketch, "E544", {"start": v(-76.63, 182.83) * mm, "mid": v(-65.33, 163.4) * mm, "end": v(-59.92, 141.59) * mm});
            skArc(sketch, "E545", {"start": v(-59.92, 141.59) * mm, "mid": v(-57.19, 102.9) * mm, "end": v(-56.86, 64.13) * mm});
            skArc(sketch, "E546", {"start": v(-502.34, -1062.66) * mm, "mid": v(-505.8, -1090.04) * mm, "end": v(-509.95, -1117.32) * mm});
            skArc(sketch, "E547", {"start": v(-509.95, -1117.32) * mm, "mid": v(-514.82, -1144.39) * mm, "end": v(-520.4, -1171.31) * mm});
            skArc(sketch, "E548", {"start": v(-520.4, -1171.31) * mm, "mid": v(-525.87, -1194.61) * mm, "end": v(-531.96, -1217.76) * mm});
            skArc(sketch, "E549", {"start": v(-531.96, -1217.76) * mm, "mid": v(-536.63, -1231.8) * mm, "end": v(-542.73, -1245.28) * mm});
            skArc(sketch, "E550", {"start": v(-542.73, -1245.28) * mm, "mid": v(-550.84, -1260.13) * mm, "end": v(-559.67, -1274.57) * mm});
            skArc(sketch, "E551", {"start": v(-559.67, -1274.57) * mm, "mid": v(-564.61, -1278.87) * mm, "end": v(-571.1, -1279.88) * mm});
            skArc(sketch, "E552", {"start": v(-571.1, -1279.88) * mm, "mid": v(-578.43, -1277.56) * mm, "end": v(-584.47, -1272.8) * mm});
            skArc(sketch, "E553", {"start": v(-584.47, -1272.8) * mm, "mid": v(-600.13, -1254.61) * mm, "end": v(-615.42, -1236.12) * mm});
            skArc(sketch, "E554", {"start": v(-615.42, -1236.12) * mm, "mid": v(-635.17, -1207.16) * mm, "end": v(-649.92, -1175.36) * mm});
            skArc(sketch, "E555", {"start": v(-649.92, -1175.36) * mm, "mid": v(-658.35, -1143.18) * mm, "end": v(-660.48, -1109.99) * mm});
            skArc(sketch, "E556", {"start": v(-660.48, -1109.99) * mm, "mid": v(-656.24, -1077.14) * mm, "end": v(-645.77, -1045.71) * mm});
            skArc(sketch, "E557", {"start": v(-645.77, -1045.71) * mm, "mid": v(-629.07, -1015.3) * mm, "end": v(-607.52, -988.1) * mm});
            skArc(sketch, "E558", {"start": v(-607.52, -988.1) * mm, "mid": v(-578.42, -959.29) * mm, "end": v(-547.3, -932.66) * mm});
            skArc(sketch, "E559", {"start": v(-547.3, -932.66) * mm, "mid": v(-530.78, -926.64) * mm, "end": v(-513.95, -931.75) * mm});
            skArc(sketch, "E560", {"start": v(-513.95, -931.75) * mm, "mid": v(-500.83, -946.94) * mm, "end": v(-496.3, -966.48) * mm});
            skArc(sketch, "E561", {"start": v(-496.3, -966.48) * mm, "mid": v(-498.14, -1014.65) * mm, "end": v(-502.34, -1062.66) * mm});
            skLineSegment(sketch, "E562.bottom", {"start": v(-472.57, -1005.4) * mm, "end": v(-426.9, -1005.4) * mm});
            skLineSegment(sketch, "E562.top", {"start": v(-472.57, -2025.1) * mm, "end": v(-426.9, -2025.1) * mm});
            skLineSegment(sketch, "E562.left", {"start": v(-472.57, -1005.4) * mm, "end": v(-472.57, -2025.1) * mm});
            skLineSegment(sketch, "E562.right", {"start": v(-426.9, -1005.4) * mm, "end": v(-426.9, -2025.1) * mm});
            skLineSegment(sketch, "E563.bottom", {"start": v(387.33, -669.1) * mm, "end": v(439.61, -669.1) * mm});
            skLineSegment(sketch, "E563.top", {"start": v(387.33, -2017.14) * mm, "end": v(439.61, -2017.14) * mm});
            skLineSegment(sketch, "E563.left", {"start": v(387.33, -669.1) * mm, "end": v(387.33, -2017.14) * mm});
            skLineSegment(sketch, "E563.right", {"start": v(439.61, -669.1) * mm, "end": v(439.61, -2017.14) * mm});
            skLineSegment(sketch, "E564", {"start": v(-472.57, -2025.1) * mm, "end": v(-446.13, -2132.09) * mm});
            skLineSegment(sketch, "E565", {"start": v(-446.13, -2132.09) * mm, "end": v(-427.05, -2025.51) * mm});
            skLineSegment(sketch, "E566", {"start": v(-427.05, -2025.51) * mm, "end": v(-472.57, -2025.1) * mm});
            skLineSegment(sketch, "E567", {"start": v(439.61, -2017.14) * mm, "end": v(419.48, -2122.06) * mm});
            skLineSegment(sketch, "E568", {"start": v(419.48, -2122.06) * mm, "end": v(387.85, -2016.93) * mm});
            skLineSegment(sketch, "E569", {"start": v(387.85, -2016.93) * mm, "end": v(439.61, -2017.14) * mm});
            skSolve(sketch);
        }
        {
            var Q0;
            Q0 = qSketchRegion(id + "F0", true);
            extrude(context, id + "F1", {"entities" : qUnion([Q0]), "depth" : 60 * mm, "offsetDistance" : 25 * mm});
        }
    });
